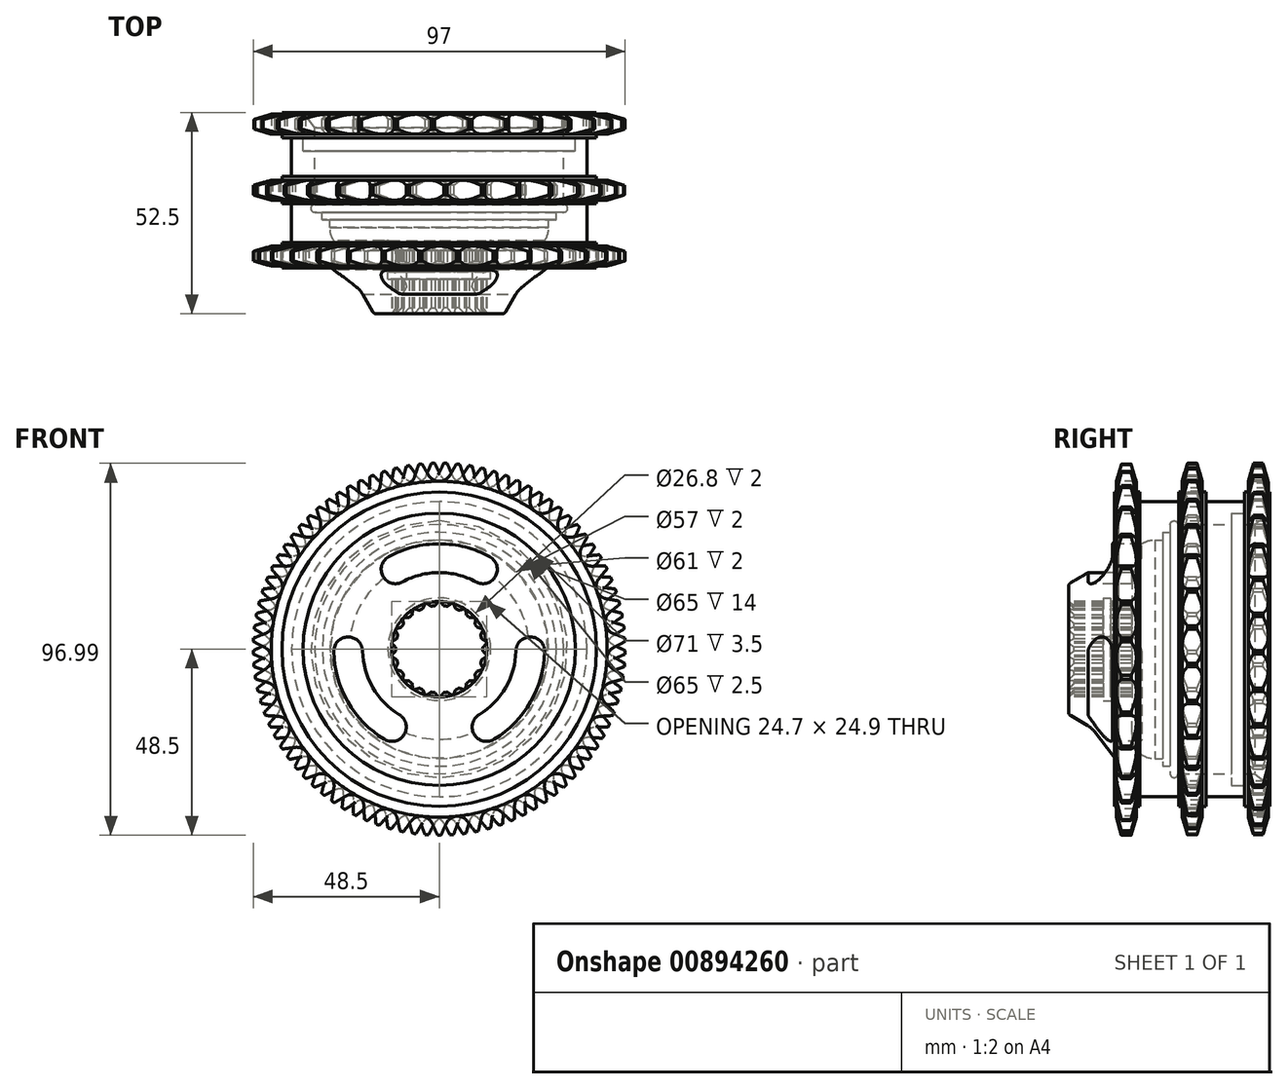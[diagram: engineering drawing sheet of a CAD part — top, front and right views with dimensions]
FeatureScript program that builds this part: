
annotation { "Feature Type Name" : "Feature", "Feature Type Description" : "" }
export const myFeature = defineFeature(function(context is Context, id is Id, definition is map)
    precondition{}
    {
        {
            var Q0;
            Q0=qCreatedBy(makeId("Right.planeOp"),FACE);
            var sketch = newSketch(context, id + "F0", { "sketchPlane" : qUnion([Q0])});
            skLineSegment(sketch, "E0.MirrorCS", {"start": v(34.85, 43.8) * mm, "end": v(34.85, 41) * mm});
            skLineSegment(sketch, "E1.MirrorCS", {"start": v(17.65, 41) * mm, "end": v(17.65, 43.8) * mm});
            skLineSegment(sketch, "E2.MirrorCS", {"start": v(5, 19.92) * mm, "end": v(0.5, 17.29) * mm});
            skLineSegment(sketch, "E3.MirrorCS", {"start": v(26.5, 32.5) * mm, "end": v(26.5, 30.5) * mm});
            skLineSegment(sketch, "E4.MirrorCS", {"start": v(35.8, 41) * mm, "end": v(34.85, 41) * mm});
            skLineSegment(sketch, "E5.MirrorCS", {"start": v(24.5, 28.5) * mm, "end": v(22.5, 28.5) * mm});
            skArc(sketch, "E6.MirrorCS", {"start": v(6.71, 21.41) * mm, "mid": v(5.93, 20.58) * mm, "end": v(5, 19.92) * mm});
            skLineSegment(sketch, "E7.MirrorCS", {"start": v(13, 34.5) * mm, "end": v(13, 31.56) * mm});
            skLineSegment(sketch, "E8.MirrorCS", {"start": v(9, 11.4) * mm, "end": v(9, 13.4) * mm});
            skLineSegment(sketch, "E9.MirrorCS", {"start": v(11, 13.4) * mm, "end": v(11, 11.4) * mm});
            skLineSegment(sketch, "E10.MirrorCS", {"start": v(33.5, 48.5) * mm, "end": v(31, 48.5) * mm});
            skArc(sketch, "E11.MirrorCS", {"start": v(12, 35.5) * mm, "mid": v(12.7, 35.2) * mm, "end": v(13, 34.5) * mm});
            skLineSegment(sketch, "E12.MirrorCS", {"start": v(29.65, 41) * mm, "end": v(28.7, 41) * mm});
            skLineSegment(sketch, "E13.MirrorCS", {"start": v(46.85, 43.8) * mm, "end": v(46.85, 41) * mm});
            skArc(sketch, "E14.MirrorCS", {"start": v(26.5, 32.5) * mm, "mid": v(27.5, 33.5) * mm, "end": v(28.5, 32.5) * mm});
            skLineSegment(sketch, "E15.MirrorCS", {"start": v(0, 12.45) * mm, "end": v(0, 16.43) * mm});
            skLineSegment(sketch, "E16.MirrorCS", {"start": v(46.85, 41) * mm, "end": v(45.9, 41) * mm});
            skLineSegment(sketch, "E17.MirrorCS", {"start": v(26.5, 30.5) * mm, "end": v(24.5, 30.5) * mm});
            skLineSegment(sketch, "E18.MirrorCS", {"start": v(1.5, 11.4) * mm, "end": v(0, 12.45) * mm});
            skLineSegment(sketch, "E19.MirrorCS", {"start": v(24.5, 30.5) * mm, "end": v(24.5, 28.5) * mm});
            skArc(sketch, "E20.MirrorCS", {"start": v(0, 16.43) * mm, "mid": v(0.13, 16.92) * mm, "end": v(0.5, 17.29) * mm});
            skLineSegment(sketch, "E21.MirrorCS", {"start": v(18.6, 41) * mm, "end": v(17.65, 41) * mm});
            skLineSegment(sketch, "E22.MirrorCS", {"start": v(29.65, 43.8) * mm, "end": v(29.65, 41) * mm});
            skLineSegment(sketch, "E23.MirrorCS", {"start": v(9, 13.4) * mm, "end": v(11, 13.4) * mm});
            skLineSegment(sketch, "E24.MirrorCS", {"start": v(18.6, 38.5) * mm, "end": v(18.6, 41) * mm});
            skLineSegment(sketch, "E25.MirrorCS", {"start": v(48.5, 32.5) * mm, "end": v(46, 32.5) * mm});
            skLineSegment(sketch, "E26.MirrorCS", {"start": v(42.5, 35.5) * mm, "end": v(46, 35.5) * mm});
            skLineSegment(sketch, "E27.MirrorCS", {"start": v(12.45, 43.8) * mm, "end": v(12.45, 41) * mm});
            skLineSegment(sketch, "E28.MirrorCS", {"start": v(52.05, 41) * mm, "end": v(52.5, 41) * mm});
            skLineSegment(sketch, "E29.MirrorCS", {"start": v(48.5, 32.5) * mm, "end": v(52.5, 35.5) * mm});
            skLineSegment(sketch, "E30.MirrorCS", {"start": v(42.5, 32.5) * mm, "end": v(42.5, 35.5) * mm});
            skArc(sketch, "E31.MirrorCS", {"start": v(13, 31.56) * mm, "mid": v(12.68, 29.61) * mm, "end": v(11.74, 27.88) * mm});
            skLineSegment(sketch, "E32.MirrorCS", {"start": v(28.7, 41) * mm, "end": v(28.7, 38.5) * mm});
            skLineSegment(sketch, "E33.MirrorCS", {"start": v(52.05, 41) * mm, "end": v(52.05, 43.8) * mm});
            skLineSegment(sketch, "E34.MirrorCS", {"start": v(46, 35.5) * mm, "end": v(46, 32.5) * mm});
            skLineSegment(sketch, "E35.MirrorCS", {"start": v(16.3, 48.5) * mm, "end": v(13.8, 48.5) * mm});
            skLineSegment(sketch, "E36.MirrorCS", {"start": v(35.8, 38.5) * mm, "end": v(35.8, 41) * mm});
            skLineSegment(sketch, "E37.MirrorCS", {"start": v(50.7, 48.5) * mm, "end": v(48.2, 48.5) * mm});
            skLineSegment(sketch, "E38.MirrorCS", {"start": v(12.45, 41) * mm, "end": v(12, 41) * mm});
            skLineSegment(sketch, "E39.MirrorCS", {"start": v(45.9, 41) * mm, "end": v(45.9, 38.5) * mm});
            skLineSegment(sketch, "E40.MirrorCS", {"start": v(33.5, 48.5) * mm, "end": v(34.85, 43.8) * mm});
            skLineSegment(sketch, "E41.MirrorCS", {"start": v(45.9, 38.5) * mm, "end": v(35.8, 38.5) * mm});
            skLineSegment(sketch, "E42.MirrorCS", {"start": v(34.85, 43.8) * mm, "end": v(29.65, 43.8) * mm, "construction": true});
            skLineSegment(sketch, "E43.MirrorCS", {"start": v(45.9, 41) * mm, "end": v(35.8, 41) * mm, "construction": true});
            skLineSegment(sketch, "E44.MirrorCS", {"start": v(12, 35.5) * mm, "end": v(12, 41) * mm});
            skLineSegment(sketch, "E45.MirrorCS", {"start": v(29.65, 43.8) * mm, "end": v(31, 48.5) * mm});
            skLineSegment(sketch, "E46.MirrorCS", {"start": v(42.5, 32.5) * mm, "end": v(28.5, 32.5) * mm});
            skLineSegment(sketch, "E47.MirrorCS", {"start": v(17.65, 43.8) * mm, "end": v(12.45, 43.8) * mm, "construction": true});
            skArc(sketch, "E48.MirrorCS", {"start": v(22.5, 28.5) * mm, "mid": v(18.58, 27.1) * mm, "end": v(16.5, 23.5) * mm});
            skLineSegment(sketch, "E49.MirrorCS", {"start": v(13.8, 48.5) * mm, "end": v(12.45, 43.8) * mm});
            skLineSegment(sketch, "E50.MirrorCS", {"start": v(53.5, 0) * mm, "end": v(0, 0) * mm, "construction": true});
            skLineSegment(sketch, "E51.MirrorCS", {"start": v(52.05, 43.8) * mm, "end": v(50.7, 48.5) * mm});
            skLineSegment(sketch, "E52.MirrorCS", {"start": v(16.3, 48.5) * mm, "end": v(17.65, 43.8) * mm});
            skLineSegment(sketch, "E53.MirrorCS", {"start": v(48.2, 48.5) * mm, "end": v(33.5, 48.5) * mm, "construction": true});
            skLineSegment(sketch, "E54.MirrorCS", {"start": v(46.85, 43.8) * mm, "end": v(48.2, 48.5) * mm});
            skLineSegment(sketch, "E55.MirrorCS", {"start": v(29.65, 43.8) * mm, "end": v(17.65, 43.8) * mm, "construction": true});
            skLineSegment(sketch, "E56.MirrorCS", {"start": v(28.7, 38.5) * mm, "end": v(18.6, 38.5) * mm});
            skLineSegment(sketch, "E57.MirrorCS", {"start": v(52.5, 41) * mm, "end": v(52.5, 35.5) * mm});
            skLineSegment(sketch, "E58.MirrorCS", {"start": v(31, 48.5) * mm, "end": v(16.3, 48.5) * mm, "construction": true});
            skLineSegment(sketch, "E59.MirrorCS", {"start": v(16.5, 11.4) * mm, "end": v(16.5, 23.5) * mm});
            skLineSegment(sketch, "E60.MirrorCS", {"start": v(46.85, 43.8) * mm, "end": v(34.85, 43.8) * mm, "construction": true});
            skLineSegment(sketch, "E61.MirrorCS", {"start": v(16.5, 11.4) * mm, "end": v(11, 11.4) * mm});
            skLineSegment(sketch, "E62.MirrorCS", {"start": v(11.74, 27.88) * mm, "end": v(6.71, 21.41) * mm});
            skLineSegment(sketch, "E63.MirrorCS", {"start": v(28.7, 41) * mm, "end": v(18.6, 41) * mm, "construction": true});
            skLineSegment(sketch, "E64.MirrorCS", {"start": v(52.05, 43.8) * mm, "end": v(46.85, 43.8) * mm, "construction": true});
            skLineSegment(sketch, "E65.MirrorCS", {"start": v(-190.05, 35.5) * mm, "end": v(-190.05, 35.5) * mm});
            skLineSegment(sketch, "E66.MirrorCS", {"start": v(9, 11.4) * mm, "end": v(1.5, 11.4) * mm});
            skSolve(sketch);
        }
        {
            var Q0;
            Q0=makeQuery(id+"F0.imprint","IMPRINT",FACE,{"disambiguationData":[TD([[makeQuery(id+"F0.imprint","IMPRINT",EDGE,{"derivedFrom":sQuery(id+"F0.wireOp",EDGE,"E0.MirrorCS")}),-1.0]])]});
            var Q1;
            Q1=sQuery(id+"F0.wireOp",EDGE,"E50.MirrorCS");
            revolve(context, id + "F1", {"surfaceOperationType" : NewSurfaceOperationType.NEW, "entities" : qUnion([Q0]), "axis" : qUnion([Q1]), "revolveType" : RevolveType.FULL});
        }
        {
            var Q0;
            Q0=makeQuery(id+"F1.opRevolve","SWEPT_FACE",FACE,{"disambiguationData":[OSD([sQuery(id+"F0.wireOp",EDGE,"E15.MirrorCS")])]});
            var sketch = newSketch(context, id + "F2", { "sketchPlane" : qUnion([Q0])});
            skArc(sketch, "E67", {"start": v(0.2, 12.45) * mm, "mid": v(0, 12.45) * mm, "end": v(-0.2, 12.45) * mm});
            skArc(sketch, "E68", {"start": v(2.1, 11.2) * mm, "mid": v(1.62, 11.28) * mm, "end": v(1.14, 11.34) * mm});
            skArc(sketch, "E69", {"start": v(5.18, 10.16) * mm, "mid": v(4.74, 10.37) * mm, "end": v(4.29, 10.56) * mm});
            skArc(sketch, "E70", {"start": v(7.83, 8.29) * mm, "mid": v(7.47, 8.62) * mm, "end": v(7.09, 8.93) * mm});
            skArc(sketch, "E71", {"start": v(9.85, 5.75) * mm, "mid": v(9.6, 6.16) * mm, "end": v(9.32, 6.57) * mm});
            skArc(sketch, "E72", {"start": v(11.07, 2.74) * mm, "mid": v(10.94, 3.21) * mm, "end": v(10.8, 3.68) * mm});
            skArc(sketch, "E73", {"start": v(11.39, -0.49) * mm, "mid": v(11.4, 0) * mm, "end": v(11.39, 0.49) * mm});
            skArc(sketch, "E74", {"start": v(10.8, -3.68) * mm, "mid": v(10.94, -3.21) * mm, "end": v(11.07, -2.74) * mm});
            skArc(sketch, "E75", {"start": v(9.32, -6.57) * mm, "mid": v(9.6, -6.16) * mm, "end": v(9.85, -5.75) * mm});
            skArc(sketch, "E76", {"start": v(7.09, -8.93) * mm, "mid": v(7.47, -8.62) * mm, "end": v(7.83, -8.29) * mm});
            skArc(sketch, "E77", {"start": v(4.29, -10.56) * mm, "mid": v(4.74, -10.37) * mm, "end": v(5.18, -10.16) * mm});
            skArc(sketch, "E78", {"start": v(1.14, -11.34) * mm, "mid": v(1.62, -11.28) * mm, "end": v(2.1, -11.2) * mm});
            skArc(sketch, "E79", {"start": v(-2.1, -11.2) * mm, "mid": v(-1.62, -11.28) * mm, "end": v(-1.14, -11.34) * mm});
            skArc(sketch, "E80", {"start": v(-5.18, -10.16) * mm, "mid": v(-4.74, -10.37) * mm, "end": v(-4.29, -10.56) * mm});
            skArc(sketch, "E81", {"start": v(-7.83, -8.29) * mm, "mid": v(-7.47, -8.62) * mm, "end": v(-7.09, -8.93) * mm});
            skArc(sketch, "E82", {"start": v(-9.85, -5.75) * mm, "mid": v(-9.6, -6.16) * mm, "end": v(-9.32, -6.57) * mm});
            skArc(sketch, "E83", {"start": v(-11.07, -2.74) * mm, "mid": v(-10.94, -3.21) * mm, "end": v(-10.8, -3.68) * mm});
            skArc(sketch, "E84", {"start": v(-11.39, 0.49) * mm, "mid": v(-11.4, 0) * mm, "end": v(-11.39, -0.49) * mm});
            skArc(sketch, "E85", {"start": v(-10.8, 3.68) * mm, "mid": v(-10.94, 3.21) * mm, "end": v(-11.07, 2.74) * mm});
            skArc(sketch, "E86", {"start": v(-9.32, 6.57) * mm, "mid": v(-9.6, 6.16) * mm, "end": v(-9.85, 5.75) * mm});
            skArc(sketch, "E87", {"start": v(-7.09, 8.93) * mm, "mid": v(-7.47, 8.62) * mm, "end": v(-7.83, 8.29) * mm});
            skArc(sketch, "E88", {"start": v(-4.29, 10.56) * mm, "mid": v(-4.74, 10.37) * mm, "end": v(-5.18, 10.16) * mm});
            skArc(sketch, "E89", {"start": v(-1.14, 11.34) * mm, "mid": v(-1.62, 11.28) * mm, "end": v(-2.1, 11.2) * mm});
            skLineSegment(sketch, "E90", {"start": v(-0.2, 12.45) * mm, "end": v(-1.14, 11.34) * mm});
            skLineSegment(sketch, "E91", {"start": v(0.2, 12.45) * mm, "end": v(1.14, 11.34) * mm});
            skArc(sketch, "E92", {"start": v(3.7, 11.89) * mm, "mid": v(3.5, 11.95) * mm, "end": v(3.31, 12) * mm});
            skLineSegment(sketch, "E93", {"start": v(3.31, 12) * mm, "end": v(2.1, 11.2) * mm});
            skLineSegment(sketch, "E94", {"start": v(3.7, 11.89) * mm, "end": v(4.29, 10.56) * mm});
            skArc(sketch, "E95", {"start": v(6.9, 10.36) * mm, "mid": v(6.73, 10.47) * mm, "end": v(6.56, 10.58) * mm});
            skLineSegment(sketch, "E96", {"start": v(6.56, 10.58) * mm, "end": v(5.18, 10.16) * mm});
            skLineSegment(sketch, "E97", {"start": v(6.9, 10.36) * mm, "end": v(7.09, 8.93) * mm});
            skArc(sketch, "E98", {"start": v(9.54, 8) * mm, "mid": v(9.4, 8.15) * mm, "end": v(9.28, 8.3) * mm});
            skLineSegment(sketch, "E99", {"start": v(9.28, 8.3) * mm, "end": v(7.83, 8.29) * mm});
            skLineSegment(sketch, "E100", {"start": v(9.54, 8) * mm, "end": v(9.32, 6.57) * mm});
            skArc(sketch, "E101", {"start": v(11.4, 4.99) * mm, "mid": v(11.32, 5.17) * mm, "end": v(11.24, 5.35) * mm});
            skLineSegment(sketch, "E102", {"start": v(11.24, 5.35) * mm, "end": v(9.85, 5.75) * mm});
            skLineSegment(sketch, "E103", {"start": v(11.4, 4.99) * mm, "end": v(10.8, 3.68) * mm});
            skArc(sketch, "E104", {"start": v(12.35, 1.57) * mm, "mid": v(12.32, 1.77) * mm, "end": v(12.3, 1.97) * mm});
            skLineSegment(sketch, "E105", {"start": v(12.3, 1.97) * mm, "end": v(11.07, 2.74) * mm});
            skLineSegment(sketch, "E106", {"start": v(12.35, 1.57) * mm, "end": v(11.39, 0.49) * mm});
            skArc(sketch, "E107", {"start": v(12.3, -1.97) * mm, "mid": v(12.32, -1.77) * mm, "end": v(12.35, -1.57) * mm});
            skLineSegment(sketch, "E108", {"start": v(12.35, -1.57) * mm, "end": v(11.39, -0.49) * mm});
            skLineSegment(sketch, "E109", {"start": v(12.3, -1.97) * mm, "end": v(11.07, -2.74) * mm});
            skArc(sketch, "E110", {"start": v(11.24, -5.35) * mm, "mid": v(11.32, -5.17) * mm, "end": v(11.4, -4.99) * mm});
            skLineSegment(sketch, "E111", {"start": v(11.4, -4.99) * mm, "end": v(10.8, -3.68) * mm});
            skLineSegment(sketch, "E112", {"start": v(11.24, -5.35) * mm, "end": v(9.85, -5.75) * mm});
            skArc(sketch, "E113", {"start": v(9.28, -8.3) * mm, "mid": v(9.4, -8.15) * mm, "end": v(9.54, -8) * mm});
            skLineSegment(sketch, "E114", {"start": v(9.54, -8) * mm, "end": v(9.32, -6.57) * mm});
            skLineSegment(sketch, "E115", {"start": v(9.28, -8.3) * mm, "end": v(7.83, -8.29) * mm});
            skArc(sketch, "E116", {"start": v(6.56, -10.58) * mm, "mid": v(6.73, -10.47) * mm, "end": v(6.9, -10.36) * mm});
            skLineSegment(sketch, "E117", {"start": v(6.9, -10.36) * mm, "end": v(7.09, -8.93) * mm});
            skLineSegment(sketch, "E118", {"start": v(6.56, -10.58) * mm, "end": v(5.18, -10.16) * mm});
            skArc(sketch, "E119", {"start": v(3.31, -12) * mm, "mid": v(3.5, -11.95) * mm, "end": v(3.7, -11.89) * mm});
            skLineSegment(sketch, "E120", {"start": v(3.7, -11.89) * mm, "end": v(4.29, -10.56) * mm});
            skLineSegment(sketch, "E121", {"start": v(3.31, -12) * mm, "end": v(2.1, -11.2) * mm});
            skArc(sketch, "E122", {"start": v(-0.2, -12.45) * mm, "mid": v(0, -12.45) * mm, "end": v(0.2, -12.45) * mm});
            skLineSegment(sketch, "E123", {"start": v(0.2, -12.45) * mm, "end": v(1.14, -11.34) * mm});
            skLineSegment(sketch, "E124", {"start": v(-0.2, -12.45) * mm, "end": v(-1.14, -11.34) * mm});
            skArc(sketch, "E125", {"start": v(-3.7, -11.89) * mm, "mid": v(-3.5, -11.95) * mm, "end": v(-3.31, -12) * mm});
            skLineSegment(sketch, "E126", {"start": v(-3.31, -12) * mm, "end": v(-2.1, -11.2) * mm});
            skLineSegment(sketch, "E127", {"start": v(-3.7, -11.89) * mm, "end": v(-4.29, -10.56) * mm});
            skArc(sketch, "E128", {"start": v(-6.9, -10.36) * mm, "mid": v(-6.73, -10.47) * mm, "end": v(-6.56, -10.58) * mm});
            skLineSegment(sketch, "E129", {"start": v(-6.56, -10.58) * mm, "end": v(-5.18, -10.16) * mm});
            skLineSegment(sketch, "E130", {"start": v(-6.9, -10.36) * mm, "end": v(-7.09, -8.93) * mm});
            skArc(sketch, "E131", {"start": v(-9.54, -8) * mm, "mid": v(-9.4, -8.15) * mm, "end": v(-9.28, -8.3) * mm});
            skLineSegment(sketch, "E132", {"start": v(-9.28, -8.3) * mm, "end": v(-7.83, -8.29) * mm});
            skLineSegment(sketch, "E133", {"start": v(-9.54, -8) * mm, "end": v(-9.32, -6.57) * mm});
            skArc(sketch, "E134", {"start": v(-11.4, -4.99) * mm, "mid": v(-11.32, -5.17) * mm, "end": v(-11.24, -5.35) * mm});
            skLineSegment(sketch, "E135", {"start": v(-11.24, -5.35) * mm, "end": v(-9.85, -5.75) * mm});
            skLineSegment(sketch, "E136", {"start": v(-11.4, -4.99) * mm, "end": v(-10.8, -3.68) * mm});
            skArc(sketch, "E137", {"start": v(-12.35, -1.57) * mm, "mid": v(-12.32, -1.77) * mm, "end": v(-12.3, -1.97) * mm});
            skLineSegment(sketch, "E138", {"start": v(-12.3, -1.97) * mm, "end": v(-11.07, -2.74) * mm});
            skLineSegment(sketch, "E139", {"start": v(-12.35, -1.57) * mm, "end": v(-11.39, -0.49) * mm});
            skArc(sketch, "E140", {"start": v(-12.3, 1.97) * mm, "mid": v(-12.32, 1.77) * mm, "end": v(-12.35, 1.57) * mm});
            skLineSegment(sketch, "E141", {"start": v(-12.35, 1.57) * mm, "end": v(-11.39, 0.49) * mm});
            skLineSegment(sketch, "E142", {"start": v(-12.3, 1.97) * mm, "end": v(-11.07, 2.74) * mm});
            skArc(sketch, "E143", {"start": v(-11.24, 5.35) * mm, "mid": v(-11.32, 5.17) * mm, "end": v(-11.4, 4.99) * mm});
            skLineSegment(sketch, "E144", {"start": v(-11.4, 4.99) * mm, "end": v(-10.8, 3.68) * mm});
            skLineSegment(sketch, "E145", {"start": v(-11.24, 5.35) * mm, "end": v(-9.85, 5.75) * mm});
            skArc(sketch, "E146", {"start": v(-9.28, 8.3) * mm, "mid": v(-9.4, 8.15) * mm, "end": v(-9.54, 8) * mm});
            skLineSegment(sketch, "E147", {"start": v(-9.54, 8) * mm, "end": v(-9.32, 6.57) * mm});
            skLineSegment(sketch, "E148", {"start": v(-9.28, 8.3) * mm, "end": v(-7.83, 8.29) * mm});
            skArc(sketch, "E149", {"start": v(-6.56, 10.58) * mm, "mid": v(-6.73, 10.47) * mm, "end": v(-6.9, 10.36) * mm});
            skLineSegment(sketch, "E150", {"start": v(-6.9, 10.36) * mm, "end": v(-7.09, 8.93) * mm});
            skLineSegment(sketch, "E151", {"start": v(-6.56, 10.58) * mm, "end": v(-5.18, 10.16) * mm});
            skArc(sketch, "E152", {"start": v(-3.31, 12) * mm, "mid": v(-3.5, 11.95) * mm, "end": v(-3.7, 11.89) * mm});
            skLineSegment(sketch, "E153", {"start": v(-3.7, 11.89) * mm, "end": v(-4.29, 10.56) * mm});
            skLineSegment(sketch, "E154", {"start": v(-3.31, 12) * mm, "end": v(-2.1, 11.2) * mm});
            skSolve(sketch);
        }
        {
            var Q0;
            Q0 = qSketchRegion(id + "F2", true);
            extrude(context, id + "F3", {"entities" : qUnion([Q0]), "operationType" : NewBodyOperationType.REMOVE, "endBound" : BoundingType.THROUGH_ALL, "oppositeDirection" : true, "depth" : 25 * mm, "offsetDistance" : 25 * mm});
        }
        {
            var Q0;
            Q0=makeQuery(id+"F1.opRevolve","SWEPT_FACE",FACE,{"disambiguationData":[OSD([sQuery(id+"F0.wireOp",EDGE,"E15.MirrorCS")])]});
            var sketch = newSketch(context, id + "F4", { "sketchPlane" : qUnion([Q0])});
            skArc(sketch, "E155", {"start": v(13.2, 24.13) * mm, "mid": v(0, 27.5) * mm, "end": v(-13.2, 24.13) * mm});
            skArc(sketch, "E156", {"start": v(9.6, 17.55) * mm, "mid": v(0, 20) * mm, "end": v(-9.6, 17.55) * mm});
            skArc(sketch, "E157", {"start": v(-13.2, 24.13) * mm, "mid": v(-14.69, 19.04) * mm, "end": v(-9.6, 17.55) * mm});
            skArc(sketch, "E158", {"start": v(9.6, 17.55) * mm, "mid": v(14.69, 19.04) * mm, "end": v(13.2, 24.13) * mm});
            skCircle(sketch, "E159", {"center": v(0, 0) * mm, "radius": 23.75 * mm, "construction": true});
            skLineSegment(sketch, "E160", {"start": v(0, 0) * mm, "end": v(11.4, 20.84) * mm, "construction": true});
            skLineSegment(sketch, "E161", {"start": v(0, 0) * mm, "end": v(-11.4, 20.84) * mm, "construction": true});
            skLineSegment(sketch, "E162", {"start": v(0, 0) * mm, "end": v(0, 23.75) * mm});
            skArc(sketch, "E163.1.0", {"start": v(-20, -0.46) * mm, "mid": v(-23.83, 3.2) * mm, "end": v(-27.5, -0.64) * mm});
            skArc(sketch, "E163.1.1", {"start": v(-27.5, -0.64) * mm, "mid": v(-23.82, -13.75) * mm, "end": v(-14.3, -23.5) * mm});
            skArc(sketch, "E163.1.2", {"start": v(-14.3, -23.5) * mm, "mid": v(-9.14, -22.24) * mm, "end": v(-10.4, -17.08) * mm});
            skArc(sketch, "E163.1.3", {"start": v(-20, -0.46) * mm, "mid": v(-17.32, -10) * mm, "end": v(-10.4, -17.08) * mm});
            skArc(sketch, "E163.2.0", {"start": v(10.4, -17.08) * mm, "mid": v(9.14, -22.24) * mm, "end": v(14.3, -23.5) * mm});
            skArc(sketch, "E163.2.1", {"start": v(14.3, -23.5) * mm, "mid": v(23.82, -13.75) * mm, "end": v(27.5, -0.64) * mm});
            skArc(sketch, "E163.2.2", {"start": v(27.5, -0.64) * mm, "mid": v(23.83, 3.2) * mm, "end": v(20, -0.46) * mm});
            skArc(sketch, "E163.2.3", {"start": v(10.4, -17.08) * mm, "mid": v(17.32, -10) * mm, "end": v(20, -0.46) * mm});
            skSolve(sketch);
        }
        {
            var Q0;
            Q0 = qSketchRegion(id + "F4", true);
            extrude(context, id + "F5", {"entities" : qUnion([Q0]), "operationType" : NewBodyOperationType.REMOVE, "endBound" : BoundingType.THROUGH_ALL, "oppositeDirection" : true, "depth" : 25 * mm, "offsetDistance" : 25 * mm});
        }
        {
            var Q0;
            Q0=makeQuery(id+"F1.opRevolve","SWEPT_FACE",FACE,{"disambiguationData":[OSD([sQuery(id+"F0.wireOp",EDGE,"E27.MirrorCS")])]});
            var sketch = newSketch(context, id + "F6", { "sketchPlane" : qUnion([Q0])});
            skArc(sketch, "E164", {"start": v(5.36, 48.2) * mm, "mid": v(4.9, 48.25) * mm, "end": v(4.45, 48.3) * mm});
            skArc(sketch, "E165", {"start": v(0, 43.8) * mm, "mid": v(1.6, 44.23) * mm, "end": v(2.77, 45.4) * mm});
            skLineSegment(sketch, "E166", {"start": v(4.46, 48.3) * mm, "end": v(2.77, 45.4) * mm});
            skArc(sketch, "E167", {"start": v(-4.45, 48.3) * mm, "mid": v(-4.9, 48.25) * mm, "end": v(-5.36, 48.2) * mm});
            skArc(sketch, "E168", {"start": v(-2.77, 45.4) * mm, "mid": v(-1.6, 44.23) * mm, "end": v(0, 43.8) * mm});
            skLineSegment(sketch, "E169", {"start": v(-4.46, 48.3) * mm, "end": v(-2.77, 45.4) * mm});
            skArc(sketch, "E170.1.0", {"start": v(-14.08, 46.41) * mm, "mid": v(-14.52, 46.28) * mm, "end": v(-14.95, 46.14) * mm});
            skLineSegment(sketch, "E170.1.1", {"start": v(-14.1, 46.42) * mm, "end": v(-11.85, 43.9) * mm});
            skArc(sketch, "E170.1.2", {"start": v(-11.85, 43.9) * mm, "mid": v(-10.47, 43) * mm, "end": v(-8.82, 42.9) * mm});
            skArc(sketch, "E170.1.3", {"start": v(-8.82, 42.9) * mm, "mid": v(-7.34, 43.64) * mm, "end": v(-6.43, 45.02) * mm});
            skLineSegment(sketch, "E170.1.4", {"start": v(-5.36, 48.22) * mm, "end": v(-6.43, 45.02) * mm});
            skArc(sketch, "E170.2.0", {"start": v(-23.14, 42.63) * mm, "mid": v(-23.54, 42.4) * mm, "end": v(-23.94, 42.18) * mm});
            skLineSegment(sketch, "E170.2.1", {"start": v(-23.15, 42.63) * mm, "end": v(-20.44, 40.62) * mm});
            skArc(sketch, "E170.2.2", {"start": v(-20.44, 40.62) * mm, "mid": v(-18.9, 40.01) * mm, "end": v(-17.27, 40.25) * mm});
            skArc(sketch, "E170.2.3", {"start": v(-17.27, 40.25) * mm, "mid": v(-15.97, 41.27) * mm, "end": v(-15.36, 42.8) * mm});
            skLineSegment(sketch, "E170.2.4", {"start": v(-14.95, 46.15) * mm, "end": v(-15.36, 42.8) * mm});
            skArc(sketch, "E170.2.5", {"start": v(-14.08, 46.41) * mm, "mid": v(-14.52, 46.28) * mm, "end": v(-14.95, 46.14) * mm});
            skArc(sketch, "E170.3.0", {"start": v(-31.24, 37.1) * mm, "mid": v(-31.6, 36.8) * mm, "end": v(-31.94, 36.5) * mm});
            skLineSegment(sketch, "E170.3.1", {"start": v(-31.26, 37.1) * mm, "end": v(-28.2, 35.68) * mm});
            skArc(sketch, "E170.3.2", {"start": v(-28.2, 35.68) * mm, "mid": v(-26.58, 35.39) * mm, "end": v(-25.02, 35.95) * mm});
            skArc(sketch, "E170.3.3", {"start": v(-25.02, 35.95) * mm, "mid": v(-23.95, 37.21) * mm, "end": v(-23.66, 38.84) * mm});
            skLineSegment(sketch, "E170.3.4", {"start": v(-23.94, 42.2) * mm, "end": v(-23.66, 38.84) * mm});
            skArc(sketch, "E170.3.5", {"start": v(-23.14, 42.63) * mm, "mid": v(-23.54, 42.4) * mm, "end": v(-23.94, 42.18) * mm});
            skArc(sketch, "E170.4.0", {"start": v(-38.07, 30.05) * mm, "mid": v(-38.35, 29.69) * mm, "end": v(-38.63, 29.32) * mm});
            skLineSegment(sketch, "E170.4.1", {"start": v(-38.09, 30.05) * mm, "end": v(-34.8, 29.27) * mm});
            skArc(sketch, "E170.4.2", {"start": v(-34.8, 29.27) * mm, "mid": v(-33.16, 29.31) * mm, "end": v(-31.75, 30.18) * mm});
            skArc(sketch, "E170.4.3", {"start": v(-31.75, 30.18) * mm, "mid": v(-30.96, 31.63) * mm, "end": v(-31, 33.28) * mm});
            skLineSegment(sketch, "E170.4.4", {"start": v(-31.94, 36.52) * mm, "end": v(-31, 33.28) * mm});
            skArc(sketch, "E170.4.5", {"start": v(-31.24, 37.1) * mm, "mid": v(-31.6, 36.8) * mm, "end": v(-31.94, 36.5) * mm});
            skArc(sketch, "E170.5.0", {"start": v(-43.34, 21.77) * mm, "mid": v(-43.54, 21.36) * mm, "end": v(-43.74, 20.95) * mm});
            skLineSegment(sketch, "E170.5.1", {"start": v(-43.36, 21.77) * mm, "end": v(-39.99, 21.66) * mm});
            skArc(sketch, "E170.5.2", {"start": v(-39.99, 21.66) * mm, "mid": v(-38.38, 22.04) * mm, "end": v(-37.17, 23.17) * mm});
            skArc(sketch, "E170.5.3", {"start": v(-37.17, 23.17) * mm, "mid": v(-36.69, 24.75) * mm, "end": v(-37.06, 26.36) * mm});
            skLineSegment(sketch, "E170.5.4", {"start": v(-38.64, 29.34) * mm, "end": v(-37.06, 26.36) * mm});
            skArc(sketch, "E170.5.5", {"start": v(-38.07, 30.05) * mm, "mid": v(-38.35, 29.69) * mm, "end": v(-38.63, 29.32) * mm});
            skArc(sketch, "E170.6.0", {"start": v(-46.84, 12.6) * mm, "mid": v(-46.95, 12.16) * mm, "end": v(-47.06, 11.71) * mm});
            skLineSegment(sketch, "E170.6.1", {"start": v(-46.85, 12.6) * mm, "end": v(-43.53, 13.17) * mm});
            skArc(sketch, "E170.6.2", {"start": v(-43.53, 13.17) * mm, "mid": v(-42.03, 13.86) * mm, "end": v(-41.07, 15.21) * mm});
            skArc(sketch, "E170.6.3", {"start": v(-41.07, 15.21) * mm, "mid": v(-40.92, 16.86) * mm, "end": v(-41.6, 18.36) * mm});
            skLineSegment(sketch, "E170.6.4", {"start": v(-43.75, 20.96) * mm, "end": v(-41.6, 18.36) * mm});
            skArc(sketch, "E170.6.5", {"start": v(-43.34, 21.77) * mm, "mid": v(-43.54, 21.36) * mm, "end": v(-43.74, 20.95) * mm});
            skArc(sketch, "E170.7.0", {"start": v(-48.41, 2.91) * mm, "mid": v(-48.44, 2.46) * mm, "end": v(-48.46, 2) * mm});
            skLineSegment(sketch, "E170.7.1", {"start": v(-48.43, 2.9) * mm, "end": v(-45.29, 4.14) * mm});
            skArc(sketch, "E170.7.2", {"start": v(-45.29, 4.14) * mm, "mid": v(-43.96, 5.12) * mm, "end": v(-43.3, 6.63) * mm});
            skArc(sketch, "E170.7.3", {"start": v(-43.3, 6.63) * mm, "mid": v(-43.48, 8.28) * mm, "end": v(-44.45, 9.6) * mm});
            skLineSegment(sketch, "E170.7.4", {"start": v(-47.08, 11.72) * mm, "end": v(-44.45, 9.6) * mm});
            skArc(sketch, "E170.7.5", {"start": v(-46.84, 12.6) * mm, "mid": v(-46.95, 12.16) * mm, "end": v(-47.06, 11.71) * mm});
            skArc(sketch, "E170.8.0", {"start": v(-48, -6.9) * mm, "mid": v(-47.94, -7.34) * mm, "end": v(-47.87, -7.8) * mm});
            skLineSegment(sketch, "E170.8.1", {"start": v(-48.02, -6.9) * mm, "end": v(-45.2, -5.06) * mm});
            skArc(sketch, "E170.8.2", {"start": v(-45.2, -5.06) * mm, "mid": v(-44.09, -3.83) * mm, "end": v(-43.74, -2.22) * mm});
            skArc(sketch, "E170.8.3", {"start": v(-43.74, -2.22) * mm, "mid": v(-44.25, -0.65) * mm, "end": v(-45.48, 0.47) * mm});
            skLineSegment(sketch, "E170.8.4", {"start": v(-48.47, 2) * mm, "end": v(-45.48, 0.47) * mm});
            skArc(sketch, "E170.8.5", {"start": v(-48.41, 2.91) * mm, "mid": v(-48.44, 2.46) * mm, "end": v(-48.46, 2) * mm});
            skArc(sketch, "E170.9.0", {"start": v(-45.64, -16.42) * mm, "mid": v(-45.48, -16.84) * mm, "end": v(-45.32, -17.27) * mm});
            skLineSegment(sketch, "E170.9.1", {"start": v(-45.65, -16.43) * mm, "end": v(-43.25, -14.06) * mm});
            skArc(sketch, "E170.9.2", {"start": v(-43.25, -14.06) * mm, "mid": v(-42.41, -12.63) * mm, "end": v(-42.4, -10.98) * mm});
            skArc(sketch, "E170.9.3", {"start": v(-42.4, -10.98) * mm, "mid": v(-43.22, -9.54) * mm, "end": v(-44.64, -8.7) * mm});
            skLineSegment(sketch, "E170.9.4", {"start": v(-47.89, -7.8) * mm, "end": v(-44.64, -8.7) * mm});
            skArc(sketch, "E170.9.5", {"start": v(-48, -6.9) * mm, "mid": v(-47.94, -7.34) * mm, "end": v(-47.87, -7.8) * mm});
            skArc(sketch, "E170.10.0", {"start": v(-41.4, -25.27) * mm, "mid": v(-41.16, -25.66) * mm, "end": v(-40.92, -26.04) * mm});
            skLineSegment(sketch, "E170.10.1", {"start": v(-41.4, -25.28) * mm, "end": v(-39.54, -22.48) * mm});
            skArc(sketch, "E170.10.2", {"start": v(-39.54, -22.48) * mm, "mid": v(-39, -20.91) * mm, "end": v(-39.32, -19.29) * mm});
            skArc(sketch, "E170.10.3", {"start": v(-39.32, -19.29) * mm, "mid": v(-40.41, -18.04) * mm, "end": v(-41.97, -17.5) * mm});
            skLineSegment(sketch, "E170.10.4", {"start": v(-45.34, -17.27) * mm, "end": v(-41.97, -17.5) * mm});
            skArc(sketch, "E170.10.5", {"start": v(-45.64, -16.42) * mm, "mid": v(-45.48, -16.84) * mm, "end": v(-45.32, -17.27) * mm});
            skArc(sketch, "E170.11.0", {"start": v(-35.47, -33.08) * mm, "mid": v(-35.15, -33.42) * mm, "end": v(-34.84, -33.74) * mm});
            skLineSegment(sketch, "E170.11.1", {"start": v(-35.47, -33.1) * mm, "end": v(-34.2, -29.97) * mm});
            skArc(sketch, "E170.11.2", {"start": v(-34.2, -29.97) * mm, "mid": v(-34, -28.33) * mm, "end": v(-34.64, -26.81) * mm});
            skArc(sketch, "E170.11.3", {"start": v(-34.64, -26.81) * mm, "mid": v(-35.95, -25.8) * mm, "end": v(-37.6, -25.6) * mm});
            skLineSegment(sketch, "E170.11.4", {"start": v(-40.93, -26.04) * mm, "end": v(-37.6, -25.6) * mm});
            skArc(sketch, "E170.11.5", {"start": v(-41.4, -25.27) * mm, "mid": v(-41.16, -25.66) * mm, "end": v(-40.92, -26.04) * mm});
            skArc(sketch, "E170.12.0", {"start": v(-28.08, -39.54) * mm, "mid": v(-27.7, -39.8) * mm, "end": v(-27.33, -40.07) * mm});
            skLineSegment(sketch, "E170.12.1", {"start": v(-28.08, -39.56) * mm, "end": v(-27.47, -36.24) * mm});
            skArc(sketch, "E170.12.2", {"start": v(-27.47, -36.24) * mm, "mid": v(-27.6, -34.6) * mm, "end": v(-28.53, -33.23) * mm});
            skArc(sketch, "E170.12.3", {"start": v(-28.53, -33.23) * mm, "mid": v(-30.02, -32.52) * mm, "end": v(-31.67, -32.64) * mm});
            skLineSegment(sketch, "E170.12.4", {"start": v(-34.85, -33.75) * mm, "end": v(-31.67, -32.64) * mm});
            skArc(sketch, "E170.12.5", {"start": v(-35.47, -33.08) * mm, "mid": v(-35.15, -33.42) * mm, "end": v(-34.84, -33.74) * mm});
            skArc(sketch, "E170.13.0", {"start": v(-19.54, -44.39) * mm, "mid": v(-19.13, -44.57) * mm, "end": v(-18.7, -44.75) * mm});
            skLineSegment(sketch, "E170.13.1", {"start": v(-19.54, -44.4) * mm, "end": v(-19.6, -41.03) * mm});
            skArc(sketch, "E170.13.2", {"start": v(-19.6, -41.03) * mm, "mid": v(-20.07, -39.44) * mm, "end": v(-21.26, -38.3) * mm});
            skArc(sketch, "E170.13.3", {"start": v(-21.26, -38.3) * mm, "mid": v(-22.86, -37.9) * mm, "end": v(-24.45, -38.35) * mm});
            skLineSegment(sketch, "E170.13.4", {"start": v(-27.34, -40.07) * mm, "end": v(-24.45, -38.35) * mm});
            skArc(sketch, "E170.13.5", {"start": v(-28.08, -39.54) * mm, "mid": v(-27.7, -39.8) * mm, "end": v(-27.33, -40.07) * mm});
            skArc(sketch, "E170.14.0", {"start": v(-10.2, -47.41) * mm, "mid": v(-9.76, -47.5) * mm, "end": v(-9.31, -47.6) * mm});
            skLineSegment(sketch, "E170.14.1", {"start": v(-10.2, -47.43) * mm, "end": v(-10.95, -44.14) * mm});
            skArc(sketch, "E170.14.2", {"start": v(-10.95, -44.14) * mm, "mid": v(-11.72, -42.68) * mm, "end": v(-13.11, -41.8) * mm});
            skArc(sketch, "E170.14.3", {"start": v(-13.11, -41.8) * mm, "mid": v(-14.76, -41.72) * mm, "end": v(-16.23, -42.48) * mm});
            skLineSegment(sketch, "E170.14.4", {"start": v(-18.72, -44.76) * mm, "end": v(-16.23, -42.48) * mm});
            skArc(sketch, "E170.14.5", {"start": v(-19.54, -44.39) * mm, "mid": v(-19.13, -44.57) * mm, "end": v(-18.7, -44.75) * mm});
            skArc(sketch, "E170.15.0", {"start": v(-0.46, -48.5) * mm, "mid": v(0, -48.5) * mm, "end": v(0.46, -48.5) * mm});
            skLineSegment(sketch, "E170.15.1", {"start": v(-0.45, -48.51) * mm, "end": v(-1.84, -45.44) * mm});
            skArc(sketch, "E170.15.2", {"start": v(-1.84, -45.44) * mm, "mid": v(-2.89, -44.16) * mm, "end": v(-4.43, -43.58) * mm});
            skArc(sketch, "E170.15.3", {"start": v(-4.43, -43.58) * mm, "mid": v(-6.06, -43.84) * mm, "end": v(-7.35, -44.88) * mm});
            skLineSegment(sketch, "E170.15.4", {"start": v(-9.32, -47.61) * mm, "end": v(-7.35, -44.88) * mm});
            skArc(sketch, "E170.15.5", {"start": v(-10.2, -47.41) * mm, "mid": v(-9.76, -47.5) * mm, "end": v(-9.31, -47.6) * mm});
            skArc(sketch, "E170.16.0", {"start": v(9.32, -47.6) * mm, "mid": v(9.76, -47.5) * mm, "end": v(10.21, -47.41) * mm});
            skLineSegment(sketch, "E170.16.1", {"start": v(9.33, -47.61) * mm, "end": v(7.35, -44.88) * mm});
            skArc(sketch, "E170.16.2", {"start": v(7.35, -44.88) * mm, "mid": v(6.06, -43.84) * mm, "end": v(4.43, -43.58) * mm});
            skArc(sketch, "E170.16.3", {"start": v(4.43, -43.58) * mm, "mid": v(2.89, -44.16) * mm, "end": v(1.84, -45.44) * mm});
            skLineSegment(sketch, "E170.16.4", {"start": v(0.45, -48.51) * mm, "end": v(1.84, -45.44) * mm});
            skArc(sketch, "E170.16.5", {"start": v(-0.46, -48.5) * mm, "mid": v(0, -48.5) * mm, "end": v(0.46, -48.5) * mm});
            skArc(sketch, "E170.17.0", {"start": v(18.7, -44.75) * mm, "mid": v(19.13, -44.57) * mm, "end": v(19.55, -44.39) * mm});
            skLineSegment(sketch, "E170.17.1", {"start": v(18.72, -44.76) * mm, "end": v(16.23, -42.48) * mm});
            skArc(sketch, "E170.17.2", {"start": v(16.23, -42.48) * mm, "mid": v(14.76, -41.72) * mm, "end": v(13.11, -41.8) * mm});
            skArc(sketch, "E170.17.3", {"start": v(13.11, -41.8) * mm, "mid": v(11.72, -42.68) * mm, "end": v(10.95, -44.14) * mm});
            skLineSegment(sketch, "E170.17.4", {"start": v(10.2, -47.43) * mm, "end": v(10.95, -44.14) * mm});
            skArc(sketch, "E170.17.5", {"start": v(9.32, -47.6) * mm, "mid": v(9.76, -47.5) * mm, "end": v(10.21, -47.41) * mm});
            skArc(sketch, "E170.18.0", {"start": v(27.33, -40.07) * mm, "mid": v(27.7, -39.8) * mm, "end": v(28.08, -39.54) * mm});
            skLineSegment(sketch, "E170.18.1", {"start": v(27.34, -40.07) * mm, "end": v(24.45, -38.35) * mm});
            skArc(sketch, "E170.18.2", {"start": v(24.45, -38.35) * mm, "mid": v(22.86, -37.9) * mm, "end": v(21.26, -38.3) * mm});
            skArc(sketch, "E170.18.3", {"start": v(21.26, -38.3) * mm, "mid": v(20.07, -39.44) * mm, "end": v(19.6, -41.03) * mm});
            skLineSegment(sketch, "E170.18.4", {"start": v(19.55, -44.4) * mm, "end": v(19.6, -41.03) * mm});
            skArc(sketch, "E170.18.5", {"start": v(18.7, -44.75) * mm, "mid": v(19.13, -44.57) * mm, "end": v(19.55, -44.39) * mm});
            skArc(sketch, "E170.19.0", {"start": v(34.84, -33.74) * mm, "mid": v(35.15, -33.41) * mm, "end": v(35.47, -33.08) * mm});
            skLineSegment(sketch, "E170.19.1", {"start": v(34.85, -33.75) * mm, "end": v(31.67, -32.64) * mm});
            skArc(sketch, "E170.19.2", {"start": v(31.67, -32.64) * mm, "mid": v(30.02, -32.52) * mm, "end": v(28.53, -33.23) * mm});
            skArc(sketch, "E170.19.3", {"start": v(28.53, -33.23) * mm, "mid": v(27.6, -34.6) * mm, "end": v(27.47, -36.25) * mm});
            skLineSegment(sketch, "E170.19.4", {"start": v(28.08, -39.56) * mm, "end": v(27.47, -36.25) * mm});
            skArc(sketch, "E170.19.5", {"start": v(27.33, -40.07) * mm, "mid": v(27.7, -39.8) * mm, "end": v(28.08, -39.54) * mm});
            skArc(sketch, "E170.20.0", {"start": v(40.92, -26.04) * mm, "mid": v(41.16, -25.65) * mm, "end": v(41.4, -25.27) * mm});
            skLineSegment(sketch, "E170.20.1", {"start": v(40.93, -26.04) * mm, "end": v(37.59, -25.6) * mm});
            skArc(sketch, "E170.20.2", {"start": v(37.59, -25.6) * mm, "mid": v(35.95, -25.8) * mm, "end": v(34.64, -26.81) * mm});
            skArc(sketch, "E170.20.3", {"start": v(34.64, -26.81) * mm, "mid": v(34, -28.33) * mm, "end": v(34.2, -29.97) * mm});
            skLineSegment(sketch, "E170.20.4", {"start": v(35.47, -33.1) * mm, "end": v(34.2, -29.97) * mm});
            skArc(sketch, "E170.20.5", {"start": v(34.84, -33.74) * mm, "mid": v(35.15, -33.41) * mm, "end": v(35.47, -33.08) * mm});
            skArc(sketch, "E170.21.0", {"start": v(45.32, -17.27) * mm, "mid": v(45.48, -16.84) * mm, "end": v(45.64, -16.41) * mm});
            skLineSegment(sketch, "E170.21.1", {"start": v(45.34, -17.27) * mm, "end": v(41.97, -17.5) * mm});
            skArc(sketch, "E170.21.2", {"start": v(41.97, -17.5) * mm, "mid": v(40.4, -18.04) * mm, "end": v(39.32, -19.29) * mm});
            skArc(sketch, "E170.21.3", {"start": v(39.32, -19.29) * mm, "mid": v(39, -20.91) * mm, "end": v(39.54, -22.48) * mm});
            skLineSegment(sketch, "E170.21.4", {"start": v(41.4, -25.28) * mm, "end": v(39.54, -22.48) * mm});
            skArc(sketch, "E170.21.5", {"start": v(40.92, -26.04) * mm, "mid": v(41.16, -25.65) * mm, "end": v(41.4, -25.27) * mm});
            skArc(sketch, "E170.22.0", {"start": v(47.87, -7.8) * mm, "mid": v(47.94, -7.34) * mm, "end": v(48, -6.9) * mm});
            skLineSegment(sketch, "E170.22.1", {"start": v(47.89, -7.8) * mm, "end": v(44.64, -8.7) * mm});
            skArc(sketch, "E170.22.2", {"start": v(44.64, -8.7) * mm, "mid": v(43.21, -9.54) * mm, "end": v(42.4, -10.98) * mm});
            skArc(sketch, "E170.22.3", {"start": v(42.4, -10.98) * mm, "mid": v(42.41, -12.63) * mm, "end": v(43.25, -14.06) * mm});
            skLineSegment(sketch, "E170.22.4", {"start": v(45.65, -16.43) * mm, "end": v(43.25, -14.06) * mm});
            skArc(sketch, "E170.22.5", {"start": v(45.32, -17.27) * mm, "mid": v(45.48, -16.84) * mm, "end": v(45.64, -16.41) * mm});
            skArc(sketch, "E170.23.0", {"start": v(48.46, 2) * mm, "mid": v(48.44, 2.46) * mm, "end": v(48.41, 2.91) * mm});
            skLineSegment(sketch, "E170.23.1", {"start": v(48.47, 2) * mm, "end": v(45.47, 0.46) * mm});
            skArc(sketch, "E170.23.2", {"start": v(45.47, 0.46) * mm, "mid": v(44.25, -0.65) * mm, "end": v(43.74, -2.22) * mm});
            skArc(sketch, "E170.23.3", {"start": v(43.74, -2.22) * mm, "mid": v(44.09, -3.83) * mm, "end": v(45.2, -5.06) * mm});
            skLineSegment(sketch, "E170.23.4", {"start": v(48.02, -6.9) * mm, "end": v(45.2, -5.06) * mm});
            skArc(sketch, "E170.23.5", {"start": v(47.87, -7.8) * mm, "mid": v(47.94, -7.34) * mm, "end": v(48, -6.9) * mm});
            skArc(sketch, "E170.24.0", {"start": v(47.06, 11.71) * mm, "mid": v(46.95, 12.16) * mm, "end": v(46.84, 12.6) * mm});
            skLineSegment(sketch, "E170.24.1", {"start": v(47.08, 11.72) * mm, "end": v(44.45, 9.6) * mm});
            skArc(sketch, "E170.24.2", {"start": v(44.45, 9.6) * mm, "mid": v(43.47, 8.28) * mm, "end": v(43.3, 6.63) * mm});
            skArc(sketch, "E170.24.3", {"start": v(43.3, 6.63) * mm, "mid": v(43.96, 5.12) * mm, "end": v(45.29, 4.14) * mm});
            skLineSegment(sketch, "E170.24.4", {"start": v(48.43, 2.9) * mm, "end": v(45.29, 4.14) * mm});
            skArc(sketch, "E170.24.5", {"start": v(48.46, 2) * mm, "mid": v(48.44, 2.46) * mm, "end": v(48.41, 2.91) * mm});
            skArc(sketch, "E170.25.0", {"start": v(43.74, 20.95) * mm, "mid": v(43.54, 21.36) * mm, "end": v(43.34, 21.77) * mm});
            skLineSegment(sketch, "E170.25.1", {"start": v(43.75, 20.96) * mm, "end": v(41.6, 18.36) * mm});
            skArc(sketch, "E170.25.2", {"start": v(41.6, 18.36) * mm, "mid": v(40.92, 16.86) * mm, "end": v(41.07, 15.21) * mm});
            skArc(sketch, "E170.25.3", {"start": v(41.07, 15.21) * mm, "mid": v(42.03, 13.86) * mm, "end": v(43.53, 13.17) * mm});
            skLineSegment(sketch, "E170.25.4", {"start": v(46.85, 12.6) * mm, "end": v(43.53, 13.17) * mm});
            skArc(sketch, "E170.25.5", {"start": v(47.06, 11.71) * mm, "mid": v(46.95, 12.16) * mm, "end": v(46.84, 12.6) * mm});
            skArc(sketch, "E170.26.0", {"start": v(38.63, 29.33) * mm, "mid": v(38.35, 29.69) * mm, "end": v(38.07, 30.05) * mm});
            skLineSegment(sketch, "E170.26.1", {"start": v(38.64, 29.34) * mm, "end": v(37.06, 26.36) * mm});
            skArc(sketch, "E170.26.2", {"start": v(37.06, 26.36) * mm, "mid": v(36.69, 24.75) * mm, "end": v(37.17, 23.17) * mm});
            skArc(sketch, "E170.26.3", {"start": v(37.17, 23.17) * mm, "mid": v(38.38, 22.04) * mm, "end": v(39.99, 21.66) * mm});
            skLineSegment(sketch, "E170.26.4", {"start": v(43.36, 21.77) * mm, "end": v(39.99, 21.66) * mm});
            skArc(sketch, "E170.26.5", {"start": v(43.74, 20.95) * mm, "mid": v(43.54, 21.36) * mm, "end": v(43.34, 21.77) * mm});
            skArc(sketch, "E170.27.0", {"start": v(31.94, 36.5) * mm, "mid": v(31.6, 36.8) * mm, "end": v(31.24, 37.1) * mm});
            skLineSegment(sketch, "E170.27.1", {"start": v(31.94, 36.52) * mm, "end": v(31, 33.28) * mm});
            skArc(sketch, "E170.27.2", {"start": v(31, 33.28) * mm, "mid": v(30.96, 31.63) * mm, "end": v(31.75, 30.18) * mm});
            skArc(sketch, "E170.27.3", {"start": v(31.75, 30.18) * mm, "mid": v(33.16, 29.31) * mm, "end": v(34.8, 29.27) * mm});
            skLineSegment(sketch, "E170.27.4", {"start": v(38.09, 30.05) * mm, "end": v(34.8, 29.27) * mm});
            skArc(sketch, "E170.27.5", {"start": v(38.63, 29.33) * mm, "mid": v(38.35, 29.69) * mm, "end": v(38.07, 30.05) * mm});
            skArc(sketch, "E170.28.0", {"start": v(23.93, 42.18) * mm, "mid": v(23.54, 42.4) * mm, "end": v(23.14, 42.63) * mm});
            skLineSegment(sketch, "E170.28.1", {"start": v(23.94, 42.2) * mm, "end": v(23.66, 38.84) * mm});
            skArc(sketch, "E170.28.2", {"start": v(23.66, 38.84) * mm, "mid": v(23.95, 37.21) * mm, "end": v(25.02, 35.95) * mm});
            skArc(sketch, "E170.28.3", {"start": v(25.02, 35.95) * mm, "mid": v(26.58, 35.39) * mm, "end": v(28.2, 35.68) * mm});
            skLineSegment(sketch, "E170.28.4", {"start": v(31.26, 37.1) * mm, "end": v(28.2, 35.68) * mm});
            skArc(sketch, "E170.28.5", {"start": v(31.94, 36.5) * mm, "mid": v(31.6, 36.8) * mm, "end": v(31.24, 37.1) * mm});
            skArc(sketch, "E170.29.0", {"start": v(14.95, 46.14) * mm, "mid": v(14.52, 46.28) * mm, "end": v(14.08, 46.41) * mm});
            skLineSegment(sketch, "E170.29.1", {"start": v(14.95, 46.15) * mm, "end": v(15.36, 42.8) * mm});
            skArc(sketch, "E170.29.2", {"start": v(15.36, 42.8) * mm, "mid": v(15.97, 41.27) * mm, "end": v(17.27, 40.25) * mm});
            skArc(sketch, "E170.29.3", {"start": v(17.27, 40.25) * mm, "mid": v(18.9, 40.01) * mm, "end": v(20.44, 40.62) * mm});
            skLineSegment(sketch, "E170.29.4", {"start": v(23.15, 42.64) * mm, "end": v(20.44, 40.62) * mm});
            skArc(sketch, "E170.29.5", {"start": v(23.93, 42.18) * mm, "mid": v(23.54, 42.4) * mm, "end": v(23.14, 42.63) * mm});
            skLineSegment(sketch, "E170.30.1", {"start": v(5.35, 48.22) * mm, "end": v(6.43, 45.02) * mm});
            skArc(sketch, "E170.30.2", {"start": v(6.43, 45.02) * mm, "mid": v(7.34, 43.64) * mm, "end": v(8.82, 42.9) * mm});
            skArc(sketch, "E170.30.3", {"start": v(8.82, 42.9) * mm, "mid": v(10.47, 43) * mm, "end": v(11.85, 43.9) * mm});
            skLineSegment(sketch, "E170.30.4", {"start": v(14.1, 46.42) * mm, "end": v(11.85, 43.9) * mm});
            skArc(sketch, "E170.30.5", {"start": v(14.95, 46.14) * mm, "mid": v(14.52, 46.28) * mm, "end": v(14.08, 46.41) * mm});
            skCircle(sketch, "E171", {"center": v(0, 0) * mm, "radius": 53.18 * mm});
            skSolve(sketch);
        }
        {
            var Q0;
            Q0 = qSketchRegion(id + "F6", true);
            extrude(context, id + "F7", {"entities" : qUnion([Q0]), "operationType" : NewBodyOperationType.REMOVE, "oppositeDirection" : true, "depth" : 6 * mm, "offsetDistance" : 25 * mm});
        }
        {
            var Q0;
            Q0=makeQuery(id+"F1.opRevolve","SWEPT_FACE",FACE,{"disambiguationData":[OSD([sQuery(id+"F0.wireOp",EDGE,"E22.MirrorCS")])]});
            var sketch = newSketch(context, id + "F8", { "sketchPlane" : qUnion([Q0])});
            skArc(sketch, "E172", {"start": v(2.1, 48.45) * mm, "mid": v(1.64, 48.47) * mm, "end": v(1.18, 48.49) * mm});
            skArc(sketch, "E173", {"start": v(-2.96, 43.7) * mm, "mid": v(-2.2, 43.85) * mm, "end": v(-1.5, 44.17) * mm});
            skArc(sketch, "E174", {"start": v(-1.5, 44.17) * mm, "mid": v(-0.8, 44.74) * mm, "end": v(-0.3, 45.48) * mm});
            skArc(sketch, "E175", {"start": v(3.37, 45.35) * mm, "mid": v(4.38, 44.04) * mm, "end": v(5.9, 43.4) * mm});
            skLineSegment(sketch, "E176", {"start": v(1.19, 48.5) * mm, "end": v(-0.3, 45.48) * mm});
            skLineSegment(sketch, "E177", {"start": v(2.09, 48.47) * mm, "end": v(3.11, 45.99) * mm});
            skLineSegment(sketch, "E178", {"start": v(3.11, 45.99) * mm, "end": v(3.37, 45.35) * mm});
            skArc(sketch, "E179.1.0", {"start": v(-11.7, 42.21) * mm, "mid": v(-10.98, 42.5) * mm, "end": v(-10.35, 42.96) * mm});
            skArc(sketch, "E179.1.1", {"start": v(-10.35, 42.96) * mm, "mid": v(-9.8, 43.66) * mm, "end": v(-9.45, 44.49) * mm});
            skLineSegment(sketch, "E179.1.2", {"start": v(-8.6, 47.75) * mm, "end": v(-9.45, 44.49) * mm});
            skArc(sketch, "E179.1.3", {"start": v(-7.7, 47.88) * mm, "mid": v(-8.15, 47.8) * mm, "end": v(-8.6, 47.73) * mm});
            skLineSegment(sketch, "E179.1.4", {"start": v(-7.71, 47.9) * mm, "end": v(-6.2, 45.67) * mm});
            skLineSegment(sketch, "E179.1.5", {"start": v(-6.2, 45.67) * mm, "end": v(-5.83, 45.1) * mm});
            skArc(sketch, "E179.1.6", {"start": v(-5.83, 45.1) * mm, "mid": v(-4.58, 44.02) * mm, "end": v(-2.96, 43.7) * mm});
            skArc(sketch, "E179.2.0", {"start": v(-19.95, 39) * mm, "mid": v(-19.3, 39.43) * mm, "end": v(-18.8, 40) * mm});
            skArc(sketch, "E179.2.1", {"start": v(-18.8, 40) * mm, "mid": v(-18.38, 40.8) * mm, "end": v(-18.21, 41.67) * mm});
            skLineSegment(sketch, "E179.2.2", {"start": v(-18.03, 45.04) * mm, "end": v(-18.21, 41.67) * mm});
            skArc(sketch, "E179.2.3", {"start": v(-17.18, 45.35) * mm, "mid": v(-17.61, 45.19) * mm, "end": v(-18.04, 45.02) * mm});
            skLineSegment(sketch, "E179.2.4", {"start": v(-17.2, 45.36) * mm, "end": v(-15.28, 43.49) * mm});
            skLineSegment(sketch, "E179.2.5", {"start": v(-15.28, 43.49) * mm, "end": v(-14.79, 43) * mm});
            skArc(sketch, "E179.2.6", {"start": v(-14.79, 43) * mm, "mid": v(-13.35, 42.2) * mm, "end": v(-11.7, 42.21) * mm});
            skArc(sketch, "E179.3.0", {"start": v(-27.4, 34.18) * mm, "mid": v(-26.85, 34.73) * mm, "end": v(-26.46, 35.4) * mm});
            skArc(sketch, "E179.3.1", {"start": v(-26.46, 35.4) * mm, "mid": v(-26.22, 36.26) * mm, "end": v(-26.23, 37.15) * mm});
            skLineSegment(sketch, "E179.3.2", {"start": v(-26.73, 40.49) * mm, "end": v(-26.23, 37.15) * mm});
            skArc(sketch, "E179.3.3", {"start": v(-25.96, 40.97) * mm, "mid": v(-26.35, 40.72) * mm, "end": v(-26.73, 40.47) * mm});
            skLineSegment(sketch, "E179.3.4", {"start": v(-25.98, 40.97) * mm, "end": v(-23.72, 39.52) * mm});
            skLineSegment(sketch, "E179.3.5", {"start": v(-23.72, 39.52) * mm, "end": v(-23.14, 39.15) * mm});
            skArc(sketch, "E179.3.6", {"start": v(-23.14, 39.15) * mm, "mid": v(-21.57, 38.65) * mm, "end": v(-19.95, 39) * mm});
            skArc(sketch, "E179.4.0", {"start": v(-33.71, 27.96) * mm, "mid": v(-33.3, 28.62) * mm, "end": v(-33.04, 29.35) * mm});
            skArc(sketch, "E179.4.1", {"start": v(-33.04, 29.35) * mm, "mid": v(-32.98, 30.24) * mm, "end": v(-33.17, 31.11) * mm});
            skLineSegment(sketch, "E179.4.2", {"start": v(-34.33, 34.28) * mm, "end": v(-33.17, 31.11) * mm});
            skArc(sketch, "E179.4.3", {"start": v(-33.68, 34.9) * mm, "mid": v(-34, 34.58) * mm, "end": v(-34.33, 34.26) * mm});
            skLineSegment(sketch, "E179.4.4", {"start": v(-33.7, 34.9) * mm, "end": v(-31.19, 33.94) * mm});
            skLineSegment(sketch, "E179.4.5", {"start": v(-31.19, 33.94) * mm, "end": v(-30.55, 33.7) * mm});
            skArc(sketch, "E179.4.6", {"start": v(-30.55, 33.7) * mm, "mid": v(-28.9, 33.51) * mm, "end": v(-27.4, 34.18) * mm});
            skArc(sketch, "E179.5.0", {"start": v(-38.65, 20.6) * mm, "mid": v(-38.37, 21.33) * mm, "end": v(-38.27, 22.1) * mm});
            skArc(sketch, "E179.5.1", {"start": v(-38.27, 22.1) * mm, "mid": v(-38.4, 22.98) * mm, "end": v(-38.75, 23.8) * mm});
            skLineSegment(sketch, "E179.5.2", {"start": v(-40.53, 26.66) * mm, "end": v(-38.75, 23.8) * mm});
            skArc(sketch, "E179.5.3", {"start": v(-40.01, 27.4) * mm, "mid": v(-40.27, 27.03) * mm, "end": v(-40.52, 26.65) * mm});
            skLineSegment(sketch, "E179.5.4", {"start": v(-40.03, 27.41) * mm, "end": v(-37.38, 26.97) * mm});
            skLineSegment(sketch, "E179.5.5", {"start": v(-37.38, 26.97) * mm, "end": v(-36.7, 26.85) * mm});
            skArc(sketch, "E179.5.6", {"start": v(-36.7, 26.85) * mm, "mid": v(-35.06, 27) * mm, "end": v(-33.71, 27.96) * mm});
            skArc(sketch, "E179.6.0", {"start": v(-42, 12.4) * mm, "mid": v(-41.88, 13.17) * mm, "end": v(-41.94, 13.94) * mm});
            skArc(sketch, "E179.6.1", {"start": v(-41.94, 13.94) * mm, "mid": v(-42.23, 14.78) * mm, "end": v(-42.75, 15.51) * mm});
            skLineSegment(sketch, "E179.6.2", {"start": v(-45.07, 17.96) * mm, "end": v(-42.75, 15.51) * mm});
            skArc(sketch, "E179.6.3", {"start": v(-44.71, 18.8) * mm, "mid": v(-44.89, 18.37) * mm, "end": v(-45.06, 17.95) * mm});
            skLineSegment(sketch, "E179.6.4", {"start": v(-44.73, 18.8) * mm, "end": v(-42.04, 18.89) * mm});
            skLineSegment(sketch, "E179.6.5", {"start": v(-42.04, 18.89) * mm, "end": v(-41.36, 18.91) * mm});
            skArc(sketch, "E179.6.6", {"start": v(-41.36, 18.91) * mm, "mid": v(-39.78, 19.4) * mm, "end": v(-38.65, 20.6) * mm});
            skArc(sketch, "E179.7.0", {"start": v(-43.64, 3.7) * mm, "mid": v(-43.67, 4.47) * mm, "end": v(-43.89, 5.21) * mm});
            skArc(sketch, "E179.7.1", {"start": v(-43.89, 5.21) * mm, "mid": v(-44.35, 5.98) * mm, "end": v(-45, 6.59) * mm});
            skLineSegment(sketch, "E179.7.2", {"start": v(-47.76, 8.52) * mm, "end": v(-45, 6.59) * mm});
            skArc(sketch, "E179.7.3", {"start": v(-47.58, 9.4) * mm, "mid": v(-47.67, 8.96) * mm, "end": v(-47.75, 8.5) * mm});
            skLineSegment(sketch, "E179.7.4", {"start": v(-47.6, 9.4) * mm, "end": v(-44.98, 10.04) * mm});
            skLineSegment(sketch, "E179.7.5", {"start": v(-44.98, 10.04) * mm, "end": v(-44.32, 10.2) * mm});
            skArc(sketch, "E179.7.6", {"start": v(-44.32, 10.2) * mm, "mid": v(-42.87, 11) * mm, "end": v(-42, 12.4) * mm});
            skArc(sketch, "E179.8.0", {"start": v(-43.5, -5.17) * mm, "mid": v(-43.68, -4.41) * mm, "end": v(-44.04, -3.73) * mm});
            skArc(sketch, "E179.8.1", {"start": v(-44.04, -3.73) * mm, "mid": v(-44.64, -3.07) * mm, "end": v(-45.4, -2.6) * mm});
            skLineSegment(sketch, "E179.8.2", {"start": v(-48.5, -1.27) * mm, "end": v(-45.4, -2.6) * mm});
            skArc(sketch, "E179.8.3", {"start": v(-48.5, -0.36) * mm, "mid": v(-48.5, -0.82) * mm, "end": v(-48.48, -1.28) * mm});
            skLineSegment(sketch, "E179.8.4", {"start": v(-48.51, -0.37) * mm, "end": v(-46.08, 0.78) * mm});
            skLineSegment(sketch, "E179.8.5", {"start": v(-46.08, 0.78) * mm, "end": v(-45.46, 1.07) * mm});
            skArc(sketch, "E179.8.6", {"start": v(-45.46, 1.07) * mm, "mid": v(-44.2, 2.14) * mm, "end": v(-43.64, 3.7) * mm});
            skArc(sketch, "E179.9.0", {"start": v(-41.56, -13.82) * mm, "mid": v(-41.9, -13.12) * mm, "end": v(-42.39, -12.52) * mm});
            skArc(sketch, "E179.9.1", {"start": v(-42.39, -12.52) * mm, "mid": v(-43.1, -12) * mm, "end": v(-43.95, -11.7) * mm});
            skLineSegment(sketch, "E179.9.2", {"start": v(-47.25, -11) * mm, "end": v(-43.95, -11.7) * mm});
            skArc(sketch, "E179.9.3", {"start": v(-47.43, -10.12) * mm, "mid": v(-47.34, -10.56) * mm, "end": v(-47.23, -11) * mm});
            skLineSegment(sketch, "E179.9.4", {"start": v(-47.45, -10.13) * mm, "end": v(-45.3, -8.51) * mm});
            skLineSegment(sketch, "E179.9.5", {"start": v(-45.3, -8.51) * mm, "end": v(-44.75, -8.1) * mm});
            skArc(sketch, "E179.9.6", {"start": v(-44.75, -8.1) * mm, "mid": v(-43.73, -6.8) * mm, "end": v(-43.5, -5.17) * mm});
            skArc(sketch, "E179.10.0", {"start": v(-37.93, -21.9) * mm, "mid": v(-38.4, -21.28) * mm, "end": v(-39, -20.8) * mm});
            skArc(sketch, "E179.10.1", {"start": v(-39, -20.8) * mm, "mid": v(-39.81, -20.43) * mm, "end": v(-40.7, -20.3) * mm});
            skLineSegment(sketch, "E179.10.2", {"start": v(-44.07, -20.3) * mm, "end": v(-40.7, -20.3) * mm});
            skArc(sketch, "E179.10.3", {"start": v(-44.43, -19.46) * mm, "mid": v(-44.24, -19.88) * mm, "end": v(-44.05, -20.3) * mm});
            skLineSegment(sketch, "E179.10.4", {"start": v(-44.44, -19.47) * mm, "end": v(-42.66, -17.46) * mm});
            skLineSegment(sketch, "E179.10.5", {"start": v(-42.66, -17.46) * mm, "end": v(-42.2, -16.94) * mm});
            skArc(sketch, "E179.10.6", {"start": v(-42.2, -16.94) * mm, "mid": v(-41.47, -15.47) * mm, "end": v(-41.56, -13.82) * mm});
            skArc(sketch, "E179.11.0", {"start": v(-32.75, -29.09) * mm, "mid": v(-33.33, -28.57) * mm, "end": v(-34.01, -28.22) * mm});
            skArc(sketch, "E179.11.1", {"start": v(-34.01, -28.22) * mm, "mid": v(-34.89, -28.02) * mm, "end": v(-35.78, -28.08) * mm});
            skLineSegment(sketch, "E179.11.2", {"start": v(-39.08, -28.75) * mm, "end": v(-35.78, -28.08) * mm});
            skArc(sketch, "E179.11.3", {"start": v(-39.6, -28) * mm, "mid": v(-39.33, -28.38) * mm, "end": v(-39.06, -28.74) * mm});
            skLineSegment(sketch, "E179.11.4", {"start": v(-39.6, -28.02) * mm, "end": v(-38.27, -25.69) * mm});
            skLineSegment(sketch, "E179.11.5", {"start": v(-38.27, -25.69) * mm, "end": v(-37.93, -25.1) * mm});
            skArc(sketch, "E179.11.6", {"start": v(-37.93, -25.1) * mm, "mid": v(-37.5, -23.5) * mm, "end": v(-37.93, -21.9) * mm});
            skArc(sketch, "E179.12.0", {"start": v(-26.22, -35.08) * mm, "mid": v(-26.9, -34.7) * mm, "end": v(-27.64, -34.49) * mm});
            skArc(sketch, "E179.12.1", {"start": v(-27.64, -34.49) * mm, "mid": v(-28.53, -34.47) * mm, "end": v(-29.4, -34.7) * mm});
            skLineSegment(sketch, "E179.12.2", {"start": v(-32.5, -36.03) * mm, "end": v(-29.4, -34.7) * mm});
            skArc(sketch, "E179.12.3", {"start": v(-33.15, -35.4) * mm, "mid": v(-32.82, -35.71) * mm, "end": v(-32.48, -36.02) * mm});
            skLineSegment(sketch, "E179.12.4", {"start": v(-33.16, -35.42) * mm, "end": v(-32.32, -32.87) * mm});
            skLineSegment(sketch, "E179.12.5", {"start": v(-32.32, -32.87) * mm, "end": v(-32.1, -32.21) * mm});
            skArc(sketch, "E179.12.6", {"start": v(-32.1, -32.21) * mm, "mid": v(-32, -30.56) * mm, "end": v(-32.75, -29.09) * mm});
            skArc(sketch, "E179.13.0", {"start": v(-18.62, -39.64) * mm, "mid": v(-19.36, -39.4) * mm, "end": v(-20.13, -39.34) * mm});
            skArc(sketch, "E179.13.1", {"start": v(-20.13, -39.34) * mm, "mid": v(-21, -39.5) * mm, "end": v(-21.8, -39.9) * mm});
            skLineSegment(sketch, "E179.13.2", {"start": v(-24.58, -41.83) * mm, "end": v(-21.8, -39.9) * mm});
            skArc(sketch, "E179.13.3", {"start": v(-25.35, -41.35) * mm, "mid": v(-24.96, -41.59) * mm, "end": v(-24.56, -41.82) * mm});
            skLineSegment(sketch, "E179.13.4", {"start": v(-25.35, -41.37) * mm, "end": v(-25.04, -38.7) * mm});
            skLineSegment(sketch, "E179.13.5", {"start": v(-25.04, -38.7) * mm, "end": v(-24.96, -38.02) * mm});
            skArc(sketch, "E179.13.6", {"start": v(-24.96, -38.02) * mm, "mid": v(-25.2, -36.38) * mm, "end": v(-26.22, -35.08) * mm});
            skArc(sketch, "E179.14.0", {"start": v(-10.26, -42.58) * mm, "mid": v(-11.03, -42.5) * mm, "end": v(-11.8, -42.6) * mm});
            skArc(sketch, "E179.14.1", {"start": v(-11.8, -42.6) * mm, "mid": v(-12.62, -42.93) * mm, "end": v(-13.32, -43.48) * mm});
            skLineSegment(sketch, "E179.14.2", {"start": v(-15.65, -45.92) * mm, "end": v(-13.32, -43.48) * mm});
            skArc(sketch, "E179.14.3", {"start": v(-16.5, -45.6) * mm, "mid": v(-16.07, -45.76) * mm, "end": v(-15.64, -45.9) * mm});
            skLineSegment(sketch, "E179.14.4", {"start": v(-16.5, -45.62) * mm, "end": v(-16.74, -42.95) * mm});
            skLineSegment(sketch, "E179.14.5", {"start": v(-16.74, -42.95) * mm, "end": v(-16.8, -42.26) * mm});
            skArc(sketch, "E179.14.6", {"start": v(-16.8, -42.26) * mm, "mid": v(-17.36, -40.7) * mm, "end": v(-18.62, -39.64) * mm});
            skArc(sketch, "E179.15.0", {"start": v(-1.48, -43.78) * mm, "mid": v(-2.25, -43.84) * mm, "end": v(-2.98, -44.1) * mm});
            skArc(sketch, "E179.15.1", {"start": v(-2.98, -44.1) * mm, "mid": v(-3.72, -44.6) * mm, "end": v(-4.3, -45.27) * mm});
            skLineSegment(sketch, "E179.15.2", {"start": v(-6.09, -48.13) * mm, "end": v(-4.3, -45.27) * mm});
            skArc(sketch, "E179.15.3", {"start": v(-6.99, -48) * mm, "mid": v(-6.53, -48.06) * mm, "end": v(-6.08, -48.12) * mm});
            skLineSegment(sketch, "E179.15.4", {"start": v(-6.98, -48) * mm, "end": v(-7.75, -45.44) * mm});
            skLineSegment(sketch, "E179.15.5", {"start": v(-7.75, -45.44) * mm, "end": v(-7.94, -44.78) * mm});
            skArc(sketch, "E179.15.6", {"start": v(-7.94, -44.78) * mm, "mid": v(-8.8, -43.37) * mm, "end": v(-10.26, -42.58) * mm});
            skArc(sketch, "E179.16.0", {"start": v(7.36, -43.18) * mm, "mid": v(6.62, -43.4) * mm, "end": v(5.95, -43.8) * mm});
            skArc(sketch, "E179.16.1", {"start": v(5.95, -43.8) * mm, "mid": v(5.33, -44.43) * mm, "end": v(4.9, -45.21) * mm});
            skLineSegment(sketch, "E179.16.2", {"start": v(3.72, -48.37) * mm, "end": v(4.9, -45.21) * mm});
            skArc(sketch, "E179.16.3", {"start": v(2.82, -48.42) * mm, "mid": v(3.27, -48.39) * mm, "end": v(3.73, -48.36) * mm});
            skLineSegment(sketch, "E179.16.4", {"start": v(2.83, -48.43) * mm, "end": v(1.56, -46.07) * mm});
            skLineSegment(sketch, "E179.16.5", {"start": v(1.56, -46.07) * mm, "end": v(1.23, -45.46) * mm});
            skArc(sketch, "E179.16.6", {"start": v(1.23, -45.46) * mm, "mid": v(0.1, -44.26) * mm, "end": v(-1.48, -43.78) * mm});
            skArc(sketch, "E179.17.0", {"start": v(15.9, -40.81) * mm, "mid": v(15.22, -41.18) * mm, "end": v(14.65, -41.7) * mm});
            skArc(sketch, "E179.17.1", {"start": v(14.65, -41.7) * mm, "mid": v(14.16, -42.45) * mm, "end": v(13.9, -43.3) * mm});
            skLineSegment(sketch, "E179.17.2", {"start": v(13.39, -46.63) * mm, "end": v(13.9, -43.3) * mm});
            skArc(sketch, "E179.17.3", {"start": v(12.5, -46.86) * mm, "mid": v(12.95, -46.74) * mm, "end": v(13.39, -46.62) * mm});
            skLineSegment(sketch, "E179.17.4", {"start": v(12.52, -46.87) * mm, "end": v(10.8, -44.8) * mm});
            skLineSegment(sketch, "E179.17.5", {"start": v(10.8, -44.8) * mm, "end": v(10.36, -44.28) * mm});
            skArc(sketch, "E179.17.6", {"start": v(10.36, -44.28) * mm, "mid": v(9, -43.33) * mm, "end": v(7.36, -43.18) * mm});
            skArc(sketch, "E179.18.0", {"start": v(23.8, -36.77) * mm, "mid": v(23.2, -37.27) * mm, "end": v(22.74, -37.9) * mm});
            skArc(sketch, "E179.18.1", {"start": v(22.74, -37.9) * mm, "mid": v(22.42, -38.73) * mm, "end": v(22.34, -39.62) * mm});
            skLineSegment(sketch, "E179.18.2", {"start": v(22.5, -42.98) * mm, "end": v(22.34, -39.62) * mm});
            skArc(sketch, "E179.18.3", {"start": v(21.68, -43.38) * mm, "mid": v(22.1, -43.18) * mm, "end": v(22.5, -42.97) * mm});
            skLineSegment(sketch, "E179.18.4", {"start": v(21.7, -43.4) * mm, "end": v(19.6, -41.72) * mm});
            skLineSegment(sketch, "E179.18.5", {"start": v(19.6, -41.72) * mm, "end": v(19.06, -41.3) * mm});
            skArc(sketch, "E179.18.6", {"start": v(19.06, -41.3) * mm, "mid": v(17.55, -40.63) * mm, "end": v(15.9, -40.81) * mm});
            skArc(sketch, "E179.19.0", {"start": v(30.7, -31.23) * mm, "mid": v(30.23, -31.84) * mm, "end": v(29.9, -32.54) * mm});
            skArc(sketch, "E179.19.1", {"start": v(29.9, -32.54) * mm, "mid": v(29.75, -33.42) * mm, "end": v(29.85, -34.3) * mm});
            skLineSegment(sketch, "E179.19.2", {"start": v(30.7, -37.57) * mm, "end": v(29.85, -34.3) * mm});
            skArc(sketch, "E179.19.3", {"start": v(29.97, -38.13) * mm, "mid": v(30.33, -37.85) * mm, "end": v(30.69, -37.56) * mm});
            skLineSegment(sketch, "E179.19.4", {"start": v(29.99, -38.14) * mm, "end": v(27.6, -36.92) * mm});
            skLineSegment(sketch, "E179.19.5", {"start": v(27.6, -36.92) * mm, "end": v(26.98, -36.6) * mm});
            skArc(sketch, "E179.19.6", {"start": v(26.98, -36.6) * mm, "mid": v(25.37, -36.27) * mm, "end": v(23.8, -36.77) * mm});
            skArc(sketch, "E179.20.0", {"start": v(36.37, -24.41) * mm, "mid": v(36.02, -25.1) * mm, "end": v(35.84, -25.86) * mm});
            skArc(sketch, "E179.20.1", {"start": v(35.84, -25.86) * mm, "mid": v(35.87, -26.75) * mm, "end": v(36.15, -27.6) * mm});
            skLineSegment(sketch, "E179.20.2", {"start": v(37.63, -30.63) * mm, "end": v(36.15, -27.6) * mm});
            skArc(sketch, "E179.20.3", {"start": v(37.04, -31.32) * mm, "mid": v(37.33, -30.97) * mm, "end": v(37.62, -30.61) * mm});
            skLineSegment(sketch, "E179.20.4", {"start": v(37.05, -31.32) * mm, "end": v(34.46, -30.6) * mm});
            skLineSegment(sketch, "E179.20.5", {"start": v(34.46, -30.6) * mm, "end": v(33.8, -30.43) * mm});
            skArc(sketch, "E179.20.6", {"start": v(33.8, -30.43) * mm, "mid": v(32.15, -30.42) * mm, "end": v(30.7, -31.23) * mm});
            skArc(sketch, "E179.21.0", {"start": v(40.54, -16.6) * mm, "mid": v(40.33, -17.34) * mm, "end": v(40.31, -18.11) * mm});
            skArc(sketch, "E179.21.1", {"start": v(40.31, -18.11) * mm, "mid": v(40.52, -18.98) * mm, "end": v(40.96, -19.76) * mm});
            skLineSegment(sketch, "E179.21.2", {"start": v(43.02, -22.43) * mm, "end": v(40.96, -19.76) * mm});
            skArc(sketch, "E179.21.3", {"start": v(42.58, -23.22) * mm, "mid": v(42.8, -22.82) * mm, "end": v(43.01, -22.41) * mm});
            skLineSegment(sketch, "E179.21.4", {"start": v(42.6, -23.22) * mm, "end": v(39.92, -23.05) * mm});
            skLineSegment(sketch, "E179.21.5", {"start": v(39.92, -23.05) * mm, "end": v(39.23, -23) * mm});
            skArc(sketch, "E179.21.6", {"start": v(39.23, -23) * mm, "mid": v(37.61, -23.32) * mm, "end": v(36.37, -24.41) * mm});
            skArc(sketch, "E179.22.0", {"start": v(43.05, -8.1) * mm, "mid": v(43, -8.86) * mm, "end": v(43.13, -9.63) * mm});
            skArc(sketch, "E179.22.1", {"start": v(43.13, -9.63) * mm, "mid": v(43.51, -10.43) * mm, "end": v(44.1, -11.1) * mm});
            skLineSegment(sketch, "E179.22.2", {"start": v(46.65, -13.3) * mm, "end": v(44.1, -11.1) * mm});
            skArc(sketch, "E179.22.3", {"start": v(46.38, -14.17) * mm, "mid": v(46.51, -13.73) * mm, "end": v(46.64, -13.3) * mm});
            skLineSegment(sketch, "E179.22.4", {"start": v(46.4, -14.17) * mm, "end": v(43.74, -14.54) * mm});
            skLineSegment(sketch, "E179.22.5", {"start": v(43.74, -14.54) * mm, "end": v(43.06, -14.63) * mm});
            skArc(sketch, "E179.22.6", {"start": v(43.06, -14.63) * mm, "mid": v(41.54, -15.27) * mm, "end": v(40.54, -16.6) * mm});
            skArc(sketch, "E179.23.0", {"start": v(43.8, 0.74) * mm, "mid": v(43.9, -0.03) * mm, "end": v(44.19, -0.75) * mm});
            skArc(sketch, "E179.23.1", {"start": v(44.19, -0.75) * mm, "mid": v(44.72, -1.46) * mm, "end": v(45.43, -2) * mm});
            skLineSegment(sketch, "E179.23.2", {"start": v(48.38, -3.64) * mm, "end": v(45.43, -2) * mm});
            skArc(sketch, "E179.23.3", {"start": v(48.29, -4.55) * mm, "mid": v(48.33, -4.1) * mm, "end": v(48.36, -3.64) * mm});
            skLineSegment(sketch, "E179.23.4", {"start": v(48.3, -4.54) * mm, "end": v(45.77, -5.44) * mm});
            skLineSegment(sketch, "E179.23.5", {"start": v(45.77, -5.44) * mm, "end": v(45.12, -5.67) * mm});
            skArc(sketch, "E179.23.6", {"start": v(45.12, -5.67) * mm, "mid": v(43.76, -6.6) * mm, "end": v(43.05, -8.1) * mm});
            skArc(sketch, "E179.24.0", {"start": v(42.75, 9.54) * mm, "mid": v(43, 8.81) * mm, "end": v(43.43, 8.16) * mm});
            skArc(sketch, "E179.24.1", {"start": v(43.43, 8.16) * mm, "mid": v(44.1, 7.57) * mm, "end": v(44.9, 7.19) * mm});
            skLineSegment(sketch, "E179.24.2", {"start": v(48.12, 6.17) * mm, "end": v(44.9, 7.19) * mm});
            skArc(sketch, "E179.24.3", {"start": v(48.21, 5.27) * mm, "mid": v(48.16, 5.72) * mm, "end": v(48.1, 6.17) * mm});
            skLineSegment(sketch, "E179.24.4", {"start": v(48.23, 5.28) * mm, "end": v(45.93, 3.89) * mm});
            skLineSegment(sketch, "E179.24.5", {"start": v(45.93, 3.89) * mm, "end": v(45.34, 3.53) * mm});
            skArc(sketch, "E179.24.6", {"start": v(45.34, 3.53) * mm, "mid": v(44.2, 2.34) * mm, "end": v(43.8, 0.74) * mm});
            skArc(sketch, "E179.25.0", {"start": v(39.95, 17.95) * mm, "mid": v(40.35, 17.29) * mm, "end": v(40.9, 16.74) * mm});
            skArc(sketch, "E179.25.1", {"start": v(40.9, 16.74) * mm, "mid": v(41.67, 16.3) * mm, "end": v(42.54, 16.08) * mm});
            skLineSegment(sketch, "E179.25.2", {"start": v(45.9, 15.73) * mm, "end": v(42.54, 16.08) * mm});
            skArc(sketch, "E179.25.3", {"start": v(46.17, 14.87) * mm, "mid": v(46.02, 15.3) * mm, "end": v(45.88, 15.73) * mm});
            skLineSegment(sketch, "E179.25.4", {"start": v(46.18, 14.88) * mm, "end": v(44.2, 13.05) * mm});
            skLineSegment(sketch, "E179.25.5", {"start": v(44.2, 13.05) * mm, "end": v(43.7, 12.59) * mm});
            skArc(sketch, "E179.25.6", {"start": v(43.7, 12.59) * mm, "mid": v(42.82, 11.2) * mm, "end": v(42.75, 9.54) * mm});
            skArc(sketch, "E179.26.0", {"start": v(35.52, 25.63) * mm, "mid": v(36.05, 25.06) * mm, "end": v(36.7, 24.63) * mm});
            skArc(sketch, "E179.26.1", {"start": v(36.7, 24.63) * mm, "mid": v(37.54, 24.35) * mm, "end": v(38.43, 24.31) * mm});
            skLineSegment(sketch, "E179.26.2", {"start": v(41.79, 24.65) * mm, "end": v(38.43, 24.31) * mm});
            skArc(sketch, "E179.26.3", {"start": v(42.23, 23.85) * mm, "mid": v(42, 24.25) * mm, "end": v(41.77, 24.65) * mm});
            skLineSegment(sketch, "E179.26.4", {"start": v(42.24, 23.87) * mm, "end": v(40.67, 21.68) * mm});
            skLineSegment(sketch, "E179.26.5", {"start": v(40.67, 21.68) * mm, "end": v(40.27, 21.13) * mm});
            skArc(sketch, "E179.26.6", {"start": v(40.27, 21.13) * mm, "mid": v(39.69, 19.58) * mm, "end": v(39.95, 17.95) * mm});
            skArc(sketch, "E179.27.0", {"start": v(29.64, 32.25) * mm, "mid": v(30.27, 31.8) * mm, "end": v(30.99, 31.51) * mm});
            skArc(sketch, "E179.27.1", {"start": v(30.99, 31.51) * mm, "mid": v(31.87, 31.4) * mm, "end": v(32.75, 31.55) * mm});
            skLineSegment(sketch, "E179.27.2", {"start": v(35.97, 32.55) * mm, "end": v(32.75, 31.55) * mm});
            skArc(sketch, "E179.27.3", {"start": v(36.56, 31.87) * mm, "mid": v(36.26, 32.2) * mm, "end": v(35.96, 32.55) * mm});
            skLineSegment(sketch, "E179.27.4", {"start": v(36.57, 31.88) * mm, "end": v(35.47, 29.43) * mm});
            skLineSegment(sketch, "E179.27.5", {"start": v(35.47, 29.43) * mm, "end": v(35.2, 28.8) * mm});
            skArc(sketch, "E179.27.6", {"start": v(35.2, 28.8) * mm, "mid": v(34.93, 27.17) * mm, "end": v(35.52, 25.63) * mm});
            skArc(sketch, "E179.28.0", {"start": v(22.54, 37.56) * mm, "mid": v(23.25, 37.24) * mm, "end": v(24, 37.1) * mm});
            skArc(sketch, "E179.28.1", {"start": v(24, 37.1) * mm, "mid": v(24.9, 37.18) * mm, "end": v(25.73, 37.5) * mm});
            skLineSegment(sketch, "E179.28.2", {"start": v(28.68, 39.13) * mm, "end": v(25.73, 37.5) * mm});
            skArc(sketch, "E179.28.3", {"start": v(29.4, 38.57) * mm, "mid": v(29.03, 38.85) * mm, "end": v(28.67, 39.12) * mm});
            skLineSegment(sketch, "E179.28.4", {"start": v(29.4, 38.59) * mm, "end": v(28.82, 35.97) * mm});
            skLineSegment(sketch, "E179.28.5", {"start": v(28.82, 35.97) * mm, "end": v(28.68, 35.3) * mm});
            skArc(sketch, "E179.28.6", {"start": v(28.68, 35.3) * mm, "mid": v(28.75, 33.65) * mm, "end": v(29.64, 32.25) * mm});
            skArc(sketch, "E179.29.0", {"start": v(14.52, 41.32) * mm, "mid": v(15.27, 41.16) * mm, "end": v(16.05, 41.18) * mm});
            skArc(sketch, "E179.29.1", {"start": v(16.05, 41.18) * mm, "mid": v(16.9, 41.43) * mm, "end": v(17.66, 41.91) * mm});
            skLineSegment(sketch, "E179.29.2", {"start": v(20.22, 44.1) * mm, "end": v(17.66, 41.91) * mm});
            skArc(sketch, "E179.29.3", {"start": v(21.03, 43.7) * mm, "mid": v(20.62, 43.9) * mm, "end": v(20.2, 44.1) * mm});
            skLineSegment(sketch, "E179.29.4", {"start": v(21.03, 43.72) * mm, "end": v(21, 41.03) * mm});
            skLineSegment(sketch, "E179.29.5", {"start": v(21, 41.03) * mm, "end": v(20.98, 40.35) * mm});
            skArc(sketch, "E179.29.6", {"start": v(20.98, 40.35) * mm, "mid": v(21.39, 38.74) * mm, "end": v(22.54, 37.56) * mm});
            skArc(sketch, "E179.30.0", {"start": v(5.9, 43.4) * mm, "mid": v(6.67, 43.4) * mm, "end": v(7.43, 43.57) * mm});
            skArc(sketch, "E179.30.1", {"start": v(7.43, 43.57) * mm, "mid": v(8.22, 43.99) * mm, "end": v(8.86, 44.6) * mm});
            skLineSegment(sketch, "E179.30.2", {"start": v(10.93, 47.27) * mm, "end": v(8.86, 44.6) * mm});
            skArc(sketch, "E179.30.3", {"start": v(11.8, 47.04) * mm, "mid": v(11.36, 47.15) * mm, "end": v(10.92, 47.26) * mm});
            skLineSegment(sketch, "E179.30.4", {"start": v(11.8, 47.06) * mm, "end": v(12.3, 44.42) * mm});
            skLineSegment(sketch, "E179.30.5", {"start": v(12.3, 44.42) * mm, "end": v(12.43, 43.74) * mm});
            skArc(sketch, "E179.30.6", {"start": v(12.43, 43.74) * mm, "mid": v(13.15, 42.26) * mm, "end": v(14.52, 41.32) * mm});
            skCircle(sketch, "E180", {"center": v(0, 0) * mm, "radius": 51.31 * mm});
            skSolve(sketch);
        }
        {
            var Q0;
            Q0 = qSketchRegion(id + "F8", true);
            extrude(context, id + "F9", {"entities" : qUnion([Q0]), "operationType" : NewBodyOperationType.REMOVE, "oppositeDirection" : true, "depth" : 6 * mm, "offsetDistance" : 25 * mm});
        }
        {
            var Q0;
            Q0=makeQuery(id+"F1.opRevolve","SWEPT_FACE",FACE,{"disambiguationData":[OSD([sQuery(id+"F0.wireOp",EDGE,"E13.MirrorCS")])]});
            var sketch = newSketch(context, id + "F10", { "sketchPlane" : qUnion([Q0])});
            skArc(sketch, "E181", {"start": v(-1.18, 48.49) * mm, "mid": v(-1.64, 48.47) * mm, "end": v(-2.1, 48.45) * mm});
            skArc(sketch, "E182", {"start": v(-5.9, 43.4) * mm, "mid": v(-4.38, 44.04) * mm, "end": v(-3.37, 45.35) * mm});
            skArc(sketch, "E183", {"start": v(0.3, 45.48) * mm, "mid": v(1.4, 44.23) * mm, "end": v(2.96, 43.7) * mm});
            skLineSegment(sketch, "E184", {"start": v(-2.09, 48.47) * mm, "end": v(-3.11, 45.99) * mm});
            skLineSegment(sketch, "E185", {"start": v(-3.11, 45.99) * mm, "end": v(-3.37, 45.35) * mm});
            skLineSegment(sketch, "E186", {"start": v(-1.19, 48.5) * mm, "end": v(0, 46.1) * mm});
            skLineSegment(sketch, "E187", {"start": v(0, 46.1) * mm, "end": v(0.3, 45.48) * mm});
            skArc(sketch, "E188.1.0", {"start": v(-14.52, 41.32) * mm, "mid": v(-13.15, 42.26) * mm, "end": v(-12.43, 43.75) * mm});
            skLineSegment(sketch, "E188.1.1", {"start": v(-12.3, 44.42) * mm, "end": v(-12.43, 43.75) * mm});
            skLineSegment(sketch, "E188.1.2", {"start": v(-11.8, 47.06) * mm, "end": v(-12.3, 44.42) * mm});
            skArc(sketch, "E188.1.3", {"start": v(-10.92, 47.26) * mm, "mid": v(-11.36, 47.15) * mm, "end": v(-11.8, 47.04) * mm});
            skLineSegment(sketch, "E188.1.4", {"start": v(-10.93, 47.27) * mm, "end": v(-9.28, 45.15) * mm});
            skLineSegment(sketch, "E188.1.5", {"start": v(-9.28, 45.15) * mm, "end": v(-8.86, 44.6) * mm});
            skArc(sketch, "E188.1.6", {"start": v(-8.86, 44.6) * mm, "mid": v(-7.54, 43.6) * mm, "end": v(-5.9, 43.4) * mm});
            skArc(sketch, "E188.2.0", {"start": v(-22.54, 37.56) * mm, "mid": v(-21.39, 38.74) * mm, "end": v(-20.98, 40.35) * mm});
            skLineSegment(sketch, "E188.2.1", {"start": v(-21, 41.03) * mm, "end": v(-20.98, 40.35) * mm});
            skLineSegment(sketch, "E188.2.2", {"start": v(-21.03, 43.72) * mm, "end": v(-21, 41.03) * mm});
            skArc(sketch, "E188.2.3", {"start": v(-20.2, 44.1) * mm, "mid": v(-20.62, 43.9) * mm, "end": v(-21.03, 43.7) * mm});
            skLineSegment(sketch, "E188.2.4", {"start": v(-20.22, 44.1) * mm, "end": v(-18.18, 42.36) * mm});
            skLineSegment(sketch, "E188.2.5", {"start": v(-18.18, 42.36) * mm, "end": v(-17.65, 41.91) * mm});
            skArc(sketch, "E188.2.6", {"start": v(-17.65, 41.91) * mm, "mid": v(-16.16, 41.2) * mm, "end": v(-14.52, 41.32) * mm});
            skArc(sketch, "E188.3.0", {"start": v(-29.64, 32.25) * mm, "mid": v(-28.75, 33.65) * mm, "end": v(-28.68, 35.3) * mm});
            skLineSegment(sketch, "E188.3.1", {"start": v(-28.82, 35.97) * mm, "end": v(-28.68, 35.3) * mm});
            skLineSegment(sketch, "E188.3.2", {"start": v(-29.4, 38.59) * mm, "end": v(-28.82, 35.97) * mm});
            skArc(sketch, "E188.3.3", {"start": v(-28.67, 39.12) * mm, "mid": v(-29.04, 38.85) * mm, "end": v(-29.4, 38.57) * mm});
            skLineSegment(sketch, "E188.3.4", {"start": v(-28.68, 39.13) * mm, "end": v(-26.33, 37.83) * mm});
            skLineSegment(sketch, "E188.3.5", {"start": v(-26.33, 37.83) * mm, "end": v(-25.73, 37.5) * mm});
            skArc(sketch, "E188.3.6", {"start": v(-25.73, 37.5) * mm, "mid": v(-24.13, 37.1) * mm, "end": v(-22.54, 37.56) * mm});
            skArc(sketch, "E188.4.0", {"start": v(-35.52, 25.63) * mm, "mid": v(-34.93, 27.17) * mm, "end": v(-35.2, 28.8) * mm});
            skLineSegment(sketch, "E188.4.1", {"start": v(-35.47, 29.43) * mm, "end": v(-35.2, 28.8) * mm});
            skLineSegment(sketch, "E188.4.2", {"start": v(-36.57, 31.88) * mm, "end": v(-35.47, 29.43) * mm});
            skArc(sketch, "E188.4.3", {"start": v(-35.96, 32.55) * mm, "mid": v(-36.26, 32.2) * mm, "end": v(-36.56, 31.87) * mm});
            skLineSegment(sketch, "E188.4.4", {"start": v(-35.97, 32.55) * mm, "end": v(-33.4, 31.76) * mm});
            skLineSegment(sketch, "E188.4.5", {"start": v(-33.4, 31.76) * mm, "end": v(-32.75, 31.55) * mm});
            skArc(sketch, "E188.4.6", {"start": v(-32.75, 31.55) * mm, "mid": v(-31.1, 31.49) * mm, "end": v(-29.64, 32.25) * mm});
            skArc(sketch, "E188.5.0", {"start": v(-39.95, 17.95) * mm, "mid": v(-39.69, 19.58) * mm, "end": v(-40.27, 21.13) * mm});
            skLineSegment(sketch, "E188.5.1", {"start": v(-40.67, 21.68) * mm, "end": v(-40.27, 21.13) * mm});
            skLineSegment(sketch, "E188.5.2", {"start": v(-42.24, 23.87) * mm, "end": v(-40.67, 21.68) * mm});
            skArc(sketch, "E188.5.3", {"start": v(-41.77, 24.64) * mm, "mid": v(-42, 24.25) * mm, "end": v(-42.23, 23.85) * mm});
            skLineSegment(sketch, "E188.5.4", {"start": v(-41.79, 24.65) * mm, "end": v(-39.12, 24.38) * mm});
            skLineSegment(sketch, "E188.5.5", {"start": v(-39.12, 24.38) * mm, "end": v(-38.43, 24.31) * mm});
            skArc(sketch, "E188.5.6", {"start": v(-38.43, 24.31) * mm, "mid": v(-36.8, 24.58) * mm, "end": v(-35.52, 25.63) * mm});
            skArc(sketch, "E188.6.0", {"start": v(-42.75, 9.54) * mm, "mid": v(-42.82, 11.2) * mm, "end": v(-43.7, 12.59) * mm});
            skLineSegment(sketch, "E188.6.1", {"start": v(-44.2, 13.05) * mm, "end": v(-43.7, 12.59) * mm});
            skLineSegment(sketch, "E188.6.2", {"start": v(-46.18, 14.87) * mm, "end": v(-44.2, 13.05) * mm});
            skArc(sketch, "E188.6.3", {"start": v(-45.88, 15.73) * mm, "mid": v(-46.02, 15.3) * mm, "end": v(-46.17, 14.86) * mm});
            skLineSegment(sketch, "E188.6.4", {"start": v(-45.9, 15.73) * mm, "end": v(-43.22, 16) * mm});
            skLineSegment(sketch, "E188.6.5", {"start": v(-43.22, 16) * mm, "end": v(-42.54, 16.08) * mm});
            skArc(sketch, "E188.6.6", {"start": v(-42.54, 16.08) * mm, "mid": v(-41, 16.67) * mm, "end": v(-39.95, 17.95) * mm});
            skArc(sketch, "E188.7.0", {"start": v(-43.8, 0.74) * mm, "mid": v(-44.2, 2.34) * mm, "end": v(-45.34, 3.53) * mm});
            skLineSegment(sketch, "E188.7.1", {"start": v(-45.93, 3.89) * mm, "end": v(-45.34, 3.53) * mm});
            skLineSegment(sketch, "E188.7.2", {"start": v(-48.23, 5.27) * mm, "end": v(-45.93, 3.89) * mm});
            skArc(sketch, "E188.7.3", {"start": v(-48.1, 6.17) * mm, "mid": v(-48.16, 5.72) * mm, "end": v(-48.21, 5.27) * mm});
            skLineSegment(sketch, "E188.7.4", {"start": v(-48.12, 6.17) * mm, "end": v(-45.56, 6.98) * mm});
            skLineSegment(sketch, "E188.7.5", {"start": v(-45.56, 6.98) * mm, "end": v(-44.9, 7.19) * mm});
            skArc(sketch, "E188.7.6", {"start": v(-44.9, 7.19) * mm, "mid": v(-43.51, 8.08) * mm, "end": v(-42.75, 9.54) * mm});
            skArc(sketch, "E188.8.0", {"start": v(-43.05, -8.1) * mm, "mid": v(-43.76, -6.6) * mm, "end": v(-45.12, -5.67) * mm});
            skLineSegment(sketch, "E188.8.1", {"start": v(-45.77, -5.44) * mm, "end": v(-45.12, -5.67) * mm});
            skLineSegment(sketch, "E188.8.2", {"start": v(-48.3, -4.54) * mm, "end": v(-45.77, -5.44) * mm});
            skArc(sketch, "E188.8.3", {"start": v(-48.36, -3.64) * mm, "mid": v(-48.33, -4.1) * mm, "end": v(-48.29, -4.55) * mm});
            skLineSegment(sketch, "E188.8.4", {"start": v(-48.38, -3.64) * mm, "end": v(-46.03, -2.33) * mm});
            skLineSegment(sketch, "E188.8.5", {"start": v(-46.03, -2.33) * mm, "end": v(-45.43, -2) * mm});
            skArc(sketch, "E188.8.6", {"start": v(-45.43, -2) * mm, "mid": v(-44.25, -0.85) * mm, "end": v(-43.8, 0.74) * mm});
            skArc(sketch, "E188.9.0", {"start": v(-40.54, -16.6) * mm, "mid": v(-41.54, -15.27) * mm, "end": v(-43.06, -14.63) * mm});
            skLineSegment(sketch, "E188.9.1", {"start": v(-43.74, -14.54) * mm, "end": v(-43.06, -14.63) * mm});
            skLineSegment(sketch, "E188.9.2", {"start": v(-46.4, -14.17) * mm, "end": v(-43.74, -14.54) * mm});
            skArc(sketch, "E188.9.3", {"start": v(-46.64, -13.3) * mm, "mid": v(-46.51, -13.74) * mm, "end": v(-46.38, -14.17) * mm});
            skLineSegment(sketch, "E188.9.4", {"start": v(-46.65, -13.3) * mm, "end": v(-44.62, -11.55) * mm});
            skLineSegment(sketch, "E188.9.5", {"start": v(-44.62, -11.55) * mm, "end": v(-44.1, -11.1) * mm});
            skArc(sketch, "E188.9.6", {"start": v(-44.1, -11.1) * mm, "mid": v(-43.17, -9.74) * mm, "end": v(-43.05, -8.1) * mm});
            skArc(sketch, "E188.10.0", {"start": v(-36.37, -24.41) * mm, "mid": v(-37.61, -23.32) * mm, "end": v(-39.23, -23) * mm});
            skLineSegment(sketch, "E188.10.1", {"start": v(-39.92, -23.05) * mm, "end": v(-39.23, -23) * mm});
            skLineSegment(sketch, "E188.10.2", {"start": v(-42.6, -23.22) * mm, "end": v(-39.92, -23.05) * mm});
            skArc(sketch, "E188.10.3", {"start": v(-43, -22.41) * mm, "mid": v(-42.8, -22.82) * mm, "end": v(-42.58, -23.22) * mm});
            skLineSegment(sketch, "E188.10.4", {"start": v(-43.02, -22.43) * mm, "end": v(-41.38, -20.3) * mm});
            skLineSegment(sketch, "E188.10.5", {"start": v(-41.38, -20.3) * mm, "end": v(-40.96, -19.75) * mm});
            skArc(sketch, "E188.10.6", {"start": v(-40.96, -19.75) * mm, "mid": v(-40.33, -18.23) * mm, "end": v(-40.54, -16.6) * mm});
            skArc(sketch, "E188.11.0", {"start": v(-30.7, -31.23) * mm, "mid": v(-32.15, -30.42) * mm, "end": v(-33.8, -30.43) * mm});
            skLineSegment(sketch, "E188.11.1", {"start": v(-34.46, -30.6) * mm, "end": v(-33.8, -30.43) * mm});
            skLineSegment(sketch, "E188.11.2", {"start": v(-37.05, -31.32) * mm, "end": v(-34.46, -30.6) * mm});
            skArc(sketch, "E188.11.3", {"start": v(-37.62, -30.61) * mm, "mid": v(-37.33, -30.97) * mm, "end": v(-37.03, -31.32) * mm});
            skLineSegment(sketch, "E188.11.4", {"start": v(-37.62, -30.63) * mm, "end": v(-36.45, -28.21) * mm});
            skLineSegment(sketch, "E188.11.5", {"start": v(-36.45, -28.21) * mm, "end": v(-36.15, -27.6) * mm});
            skArc(sketch, "E188.11.6", {"start": v(-36.15, -27.6) * mm, "mid": v(-35.83, -25.97) * mm, "end": v(-36.37, -24.41) * mm});
            skArc(sketch, "E188.12.0", {"start": v(-23.8, -36.77) * mm, "mid": v(-25.37, -36.26) * mm, "end": v(-26.98, -36.6) * mm});
            skLineSegment(sketch, "E188.12.1", {"start": v(-27.6, -36.92) * mm, "end": v(-26.98, -36.6) * mm});
            skLineSegment(sketch, "E188.12.2", {"start": v(-29.99, -38.14) * mm, "end": v(-27.6, -36.92) * mm});
            skArc(sketch, "E188.12.3", {"start": v(-30.69, -37.56) * mm, "mid": v(-30.33, -37.85) * mm, "end": v(-29.97, -38.13) * mm});
            skLineSegment(sketch, "E188.12.4", {"start": v(-30.69, -37.57) * mm, "end": v(-30.02, -34.97) * mm});
            skLineSegment(sketch, "E188.12.5", {"start": v(-30.02, -34.97) * mm, "end": v(-29.85, -34.3) * mm});
            skArc(sketch, "E188.12.6", {"start": v(-29.85, -34.3) * mm, "mid": v(-29.87, -32.66) * mm, "end": v(-30.7, -31.23) * mm});
            skArc(sketch, "E188.13.0", {"start": v(-15.9, -40.81) * mm, "mid": v(-17.55, -40.63) * mm, "end": v(-19.06, -41.3) * mm});
            skLineSegment(sketch, "E188.13.1", {"start": v(-19.6, -41.72) * mm, "end": v(-19.06, -41.3) * mm});
            skLineSegment(sketch, "E188.13.2", {"start": v(-21.7, -43.4) * mm, "end": v(-19.6, -41.72) * mm});
            skArc(sketch, "E188.13.3", {"start": v(-22.5, -42.97) * mm, "mid": v(-22.1, -43.18) * mm, "end": v(-21.68, -43.38) * mm});
            skLineSegment(sketch, "E188.13.4", {"start": v(-22.5, -42.98) * mm, "end": v(-22.37, -40.3) * mm});
            skLineSegment(sketch, "E188.13.5", {"start": v(-22.37, -40.3) * mm, "end": v(-22.34, -39.61) * mm});
            skArc(sketch, "E188.13.6", {"start": v(-22.34, -39.61) * mm, "mid": v(-22.68, -38) * mm, "end": v(-23.8, -36.77) * mm});
            skArc(sketch, "E188.14.0", {"start": v(-7.36, -43.18) * mm, "mid": v(-9, -43.33) * mm, "end": v(-10.36, -44.28) * mm});
            skLineSegment(sketch, "E188.14.1", {"start": v(-10.8, -44.8) * mm, "end": v(-10.36, -44.28) * mm});
            skLineSegment(sketch, "E188.14.2", {"start": v(-12.52, -46.87) * mm, "end": v(-10.8, -44.8) * mm});
            skArc(sketch, "E188.14.3", {"start": v(-13.39, -46.62) * mm, "mid": v(-12.95, -46.74) * mm, "end": v(-12.5, -46.86) * mm});
            skLineSegment(sketch, "E188.14.4", {"start": v(-13.38, -46.63) * mm, "end": v(-13.8, -43.98) * mm});
            skLineSegment(sketch, "E188.14.5", {"start": v(-13.8, -43.98) * mm, "end": v(-13.9, -43.3) * mm});
            skArc(sketch, "E188.14.6", {"start": v(-13.9, -43.3) * mm, "mid": v(-14.57, -41.79) * mm, "end": v(-15.9, -40.81) * mm});
            skArc(sketch, "E188.15.0", {"start": v(1.48, -43.78) * mm, "mid": v(-0.1, -44.26) * mm, "end": v(-1.23, -45.46) * mm});
            skLineSegment(sketch, "E188.15.1", {"start": v(-1.56, -46.07) * mm, "end": v(-1.23, -45.46) * mm});
            skLineSegment(sketch, "E188.15.2", {"start": v(-2.83, -48.43) * mm, "end": v(-1.56, -46.07) * mm});
            skArc(sketch, "E188.15.3", {"start": v(-3.73, -48.36) * mm, "mid": v(-3.27, -48.39) * mm, "end": v(-2.82, -48.42) * mm});
            skLineSegment(sketch, "E188.15.4", {"start": v(-3.72, -48.37) * mm, "end": v(-4.66, -45.85) * mm});
            skLineSegment(sketch, "E188.15.5", {"start": v(-4.66, -45.85) * mm, "end": v(-4.9, -45.21) * mm});
            skArc(sketch, "E188.15.6", {"start": v(-4.9, -45.21) * mm, "mid": v(-5.86, -43.87) * mm, "end": v(-7.36, -43.18) * mm});
            skArc(sketch, "E188.16.0", {"start": v(10.26, -42.58) * mm, "mid": v(8.8, -43.37) * mm, "end": v(7.94, -44.78) * mm});
            skLineSegment(sketch, "E188.16.1", {"start": v(7.75, -45.44) * mm, "end": v(7.94, -44.78) * mm});
            skLineSegment(sketch, "E188.16.2", {"start": v(6.98, -48) * mm, "end": v(7.75, -45.44) * mm});
            skArc(sketch, "E188.16.3", {"start": v(6.08, -48.12) * mm, "mid": v(6.53, -48.06) * mm, "end": v(6.99, -48) * mm});
            skLineSegment(sketch, "E188.16.4", {"start": v(6.09, -48.13) * mm, "end": v(4.66, -45.85) * mm});
            skLineSegment(sketch, "E188.16.5", {"start": v(4.66, -45.85) * mm, "end": v(4.3, -45.27) * mm});
            skArc(sketch, "E188.16.6", {"start": v(4.3, -45.27) * mm, "mid": v(3.09, -44.15) * mm, "end": v(1.48, -43.78) * mm});
            skArc(sketch, "E188.17.0", {"start": v(18.62, -39.64) * mm, "mid": v(17.36, -40.7) * mm, "end": v(16.8, -42.26) * mm});
            skLineSegment(sketch, "E188.17.1", {"start": v(16.74, -42.95) * mm, "end": v(16.8, -42.26) * mm});
            skLineSegment(sketch, "E188.17.2", {"start": v(16.5, -45.62) * mm, "end": v(16.74, -42.95) * mm});
            skArc(sketch, "E188.17.3", {"start": v(15.64, -45.9) * mm, "mid": v(16.07, -45.76) * mm, "end": v(16.5, -45.6) * mm});
            skLineSegment(sketch, "E188.17.4", {"start": v(15.65, -45.92) * mm, "end": v(13.8, -43.98) * mm});
            skLineSegment(sketch, "E188.17.5", {"start": v(13.8, -43.98) * mm, "end": v(13.32, -43.48) * mm});
            skArc(sketch, "E188.17.6", {"start": v(13.32, -43.48) * mm, "mid": v(11.91, -42.62) * mm, "end": v(10.26, -42.58) * mm});
            skArc(sketch, "E188.18.0", {"start": v(26.22, -35.08) * mm, "mid": v(25.2, -36.38) * mm, "end": v(24.96, -38.02) * mm});
            skLineSegment(sketch, "E188.18.1", {"start": v(25.04, -38.7) * mm, "end": v(24.96, -38.02) * mm});
            skLineSegment(sketch, "E188.18.2", {"start": v(25.35, -41.37) * mm, "end": v(25.04, -38.7) * mm});
            skArc(sketch, "E188.18.3", {"start": v(24.56, -41.82) * mm, "mid": v(24.96, -41.59) * mm, "end": v(25.35, -41.35) * mm});
            skLineSegment(sketch, "E188.18.4", {"start": v(24.58, -41.83) * mm, "end": v(22.37, -40.3) * mm});
            skLineSegment(sketch, "E188.18.5", {"start": v(22.37, -40.3) * mm, "end": v(21.8, -39.9) * mm});
            skArc(sketch, "E188.18.6", {"start": v(21.8, -39.9) * mm, "mid": v(20.25, -39.35) * mm, "end": v(18.62, -39.64) * mm});
            skArc(sketch, "E188.19.0", {"start": v(32.75, -29.09) * mm, "mid": v(32, -30.56) * mm, "end": v(32.1, -32.22) * mm});
            skLineSegment(sketch, "E188.19.1", {"start": v(32.32, -32.87) * mm, "end": v(32.1, -32.22) * mm});
            skLineSegment(sketch, "E188.19.2", {"start": v(33.16, -35.42) * mm, "end": v(32.32, -32.87) * mm});
            skArc(sketch, "E188.19.3", {"start": v(32.48, -36.02) * mm, "mid": v(32.82, -35.71) * mm, "end": v(33.15, -35.4) * mm});
            skLineSegment(sketch, "E188.19.4", {"start": v(32.5, -36.03) * mm, "end": v(30.02, -34.97) * mm});
            skLineSegment(sketch, "E188.19.5", {"start": v(30.02, -34.97) * mm, "end": v(29.4, -34.7) * mm});
            skArc(sketch, "E188.19.6", {"start": v(29.4, -34.7) * mm, "mid": v(27.76, -34.47) * mm, "end": v(26.22, -35.08) * mm});
            skArc(sketch, "E188.20.0", {"start": v(37.93, -21.9) * mm, "mid": v(37.5, -23.5) * mm, "end": v(37.93, -25.1) * mm});
            skLineSegment(sketch, "E188.20.1", {"start": v(38.27, -25.69) * mm, "end": v(37.93, -25.1) * mm});
            skLineSegment(sketch, "E188.20.2", {"start": v(39.6, -28.02) * mm, "end": v(38.27, -25.69) * mm});
            skArc(sketch, "E188.20.3", {"start": v(39.06, -28.74) * mm, "mid": v(39.33, -28.37) * mm, "end": v(39.6, -28) * mm});
            skLineSegment(sketch, "E188.20.4", {"start": v(39.08, -28.75) * mm, "end": v(36.45, -28.21) * mm});
            skLineSegment(sketch, "E188.20.5", {"start": v(36.45, -28.21) * mm, "end": v(35.78, -28.08) * mm});
            skArc(sketch, "E188.20.6", {"start": v(35.78, -28.08) * mm, "mid": v(34.13, -28.18) * mm, "end": v(32.75, -29.09) * mm});
            skArc(sketch, "E188.21.0", {"start": v(41.56, -13.82) * mm, "mid": v(41.47, -15.47) * mm, "end": v(42.2, -16.95) * mm});
            skLineSegment(sketch, "E188.21.1", {"start": v(42.66, -17.46) * mm, "end": v(42.2, -16.95) * mm});
            skLineSegment(sketch, "E188.21.2", {"start": v(44.44, -19.47) * mm, "end": v(42.66, -17.46) * mm});
            skArc(sketch, "E188.21.3", {"start": v(44.05, -20.3) * mm, "mid": v(44.24, -19.88) * mm, "end": v(44.43, -19.46) * mm});
            skLineSegment(sketch, "E188.21.4", {"start": v(44.07, -20.3) * mm, "end": v(41.38, -20.3) * mm});
            skLineSegment(sketch, "E188.21.5", {"start": v(41.38, -20.3) * mm, "end": v(40.7, -20.3) * mm});
            skArc(sketch, "E188.21.6", {"start": v(40.7, -20.3) * mm, "mid": v(39.1, -20.73) * mm, "end": v(37.93, -21.9) * mm});
            skArc(sketch, "E188.22.0", {"start": v(43.5, -5.17) * mm, "mid": v(43.73, -6.8) * mm, "end": v(44.75, -8.1) * mm});
            skLineSegment(sketch, "E188.22.1", {"start": v(45.3, -8.51) * mm, "end": v(44.75, -8.1) * mm});
            skLineSegment(sketch, "E188.22.2", {"start": v(47.45, -10.13) * mm, "end": v(45.3, -8.51) * mm});
            skArc(sketch, "E188.22.3", {"start": v(47.23, -11) * mm, "mid": v(47.34, -10.56) * mm, "end": v(47.43, -10.12) * mm});
            skLineSegment(sketch, "E188.22.4", {"start": v(47.25, -11) * mm, "end": v(44.62, -11.55) * mm});
            skLineSegment(sketch, "E188.22.5", {"start": v(44.62, -11.55) * mm, "end": v(43.95, -11.7) * mm});
            skArc(sketch, "E188.22.6", {"start": v(43.95, -11.7) * mm, "mid": v(42.47, -12.44) * mm, "end": v(41.56, -13.82) * mm});
            skArc(sketch, "E188.23.0", {"start": v(43.64, 3.7) * mm, "mid": v(44.2, 2.14) * mm, "end": v(45.47, 1.07) * mm});
            skLineSegment(sketch, "E188.23.1", {"start": v(46.08, 0.78) * mm, "end": v(45.47, 1.07) * mm});
            skLineSegment(sketch, "E188.23.2", {"start": v(48.51, -0.37) * mm, "end": v(46.08, 0.78) * mm});
            skArc(sketch, "E188.23.3", {"start": v(48.48, -1.28) * mm, "mid": v(48.5, -0.82) * mm, "end": v(48.5, -0.36) * mm});
            skLineSegment(sketch, "E188.23.4", {"start": v(48.5, -1.27) * mm, "end": v(46.03, -2.33) * mm});
            skLineSegment(sketch, "E188.23.5", {"start": v(46.03, -2.33) * mm, "end": v(45.4, -2.6) * mm});
            skArc(sketch, "E188.23.6", {"start": v(45.4, -2.6) * mm, "mid": v(44.1, -3.63) * mm, "end": v(43.5, -5.17) * mm});
            skArc(sketch, "E188.24.0", {"start": v(42, 12.4) * mm, "mid": v(42.87, 11) * mm, "end": v(44.32, 10.2) * mm});
            skLineSegment(sketch, "E188.24.1", {"start": v(44.98, 10.04) * mm, "end": v(44.32, 10.2) * mm});
            skLineSegment(sketch, "E188.24.2", {"start": v(47.6, 9.4) * mm, "end": v(44.98, 10.04) * mm});
            skArc(sketch, "E188.24.3", {"start": v(47.75, 8.51) * mm, "mid": v(47.67, 8.96) * mm, "end": v(47.58, 9.4) * mm});
            skLineSegment(sketch, "E188.24.4", {"start": v(47.76, 8.52) * mm, "end": v(45.56, 6.98) * mm});
            skLineSegment(sketch, "E188.24.5", {"start": v(45.56, 6.98) * mm, "end": v(45, 6.59) * mm});
            skArc(sketch, "E188.24.6", {"start": v(45, 6.59) * mm, "mid": v(43.93, 5.32) * mm, "end": v(43.64, 3.7) * mm});
            skArc(sketch, "E188.25.0", {"start": v(38.65, 20.6) * mm, "mid": v(39.78, 19.4) * mm, "end": v(41.36, 18.91) * mm});
            skLineSegment(sketch, "E188.25.1", {"start": v(42.04, 18.89) * mm, "end": v(41.36, 18.91) * mm});
            skLineSegment(sketch, "E188.25.2", {"start": v(44.73, 18.8) * mm, "end": v(42.04, 18.89) * mm});
            skArc(sketch, "E188.25.3", {"start": v(45.06, 17.95) * mm, "mid": v(44.89, 18.37) * mm, "end": v(44.71, 18.8) * mm});
            skLineSegment(sketch, "E188.25.4", {"start": v(45.07, 17.96) * mm, "end": v(43.22, 16) * mm});
            skLineSegment(sketch, "E188.25.5", {"start": v(43.22, 16) * mm, "end": v(42.75, 15.5) * mm});
            skArc(sketch, "E188.25.6", {"start": v(42.75, 15.5) * mm, "mid": v(41.96, 14.06) * mm, "end": v(42, 12.4) * mm});
            skArc(sketch, "E188.26.0", {"start": v(33.71, 27.96) * mm, "mid": v(35.06, 27) * mm, "end": v(36.7, 26.85) * mm});
            skLineSegment(sketch, "E188.26.1", {"start": v(37.38, 26.97) * mm, "end": v(36.7, 26.85) * mm});
            skLineSegment(sketch, "E188.26.2", {"start": v(40.03, 27.41) * mm, "end": v(37.38, 26.97) * mm});
            skArc(sketch, "E188.26.3", {"start": v(40.52, 26.65) * mm, "mid": v(40.27, 27.03) * mm, "end": v(40.01, 27.4) * mm});
            skLineSegment(sketch, "E188.26.4", {"start": v(40.53, 26.66) * mm, "end": v(39.12, 24.38) * mm});
            skLineSegment(sketch, "E188.26.5", {"start": v(39.12, 24.38) * mm, "end": v(38.75, 23.8) * mm});
            skArc(sketch, "E188.26.6", {"start": v(38.75, 23.8) * mm, "mid": v(38.28, 22.22) * mm, "end": v(38.65, 20.6) * mm});
            skArc(sketch, "E188.27.0", {"start": v(27.4, 34.18) * mm, "mid": v(28.9, 33.51) * mm, "end": v(30.55, 33.7) * mm});
            skLineSegment(sketch, "E188.27.1", {"start": v(31.19, 33.94) * mm, "end": v(30.55, 33.7) * mm});
            skLineSegment(sketch, "E188.27.2", {"start": v(33.7, 34.9) * mm, "end": v(31.19, 33.94) * mm});
            skArc(sketch, "E188.27.3", {"start": v(34.33, 34.26) * mm, "mid": v(34, 34.58) * mm, "end": v(33.68, 34.9) * mm});
            skLineSegment(sketch, "E188.27.4", {"start": v(34.33, 34.28) * mm, "end": v(33.4, 31.76) * mm});
            skLineSegment(sketch, "E188.27.5", {"start": v(33.4, 31.76) * mm, "end": v(33.17, 31.11) * mm});
            skArc(sketch, "E188.27.6", {"start": v(33.17, 31.11) * mm, "mid": v(33.02, 29.47) * mm, "end": v(33.71, 27.96) * mm});
            skArc(sketch, "E188.28.0", {"start": v(19.95, 39) * mm, "mid": v(21.57, 38.65) * mm, "end": v(23.14, 39.15) * mm});
            skLineSegment(sketch, "E188.28.1", {"start": v(23.72, 39.52) * mm, "end": v(23.14, 39.15) * mm});
            skLineSegment(sketch, "E188.28.2", {"start": v(25.97, 40.98) * mm, "end": v(23.72, 39.52) * mm});
            skArc(sketch, "E188.28.3", {"start": v(26.73, 40.47) * mm, "mid": v(26.35, 40.72) * mm, "end": v(25.96, 40.97) * mm});
            skLineSegment(sketch, "E188.28.4", {"start": v(26.73, 40.49) * mm, "end": v(26.33, 37.83) * mm});
            skLineSegment(sketch, "E188.28.5", {"start": v(26.33, 37.83) * mm, "end": v(26.23, 37.15) * mm});
            skArc(sketch, "E188.28.6", {"start": v(26.23, 37.15) * mm, "mid": v(26.41, 35.5) * mm, "end": v(27.4, 34.18) * mm});
            skArc(sketch, "E188.29.0", {"start": v(11.7, 42.21) * mm, "mid": v(13.35, 42.2) * mm, "end": v(14.79, 43) * mm});
            skLineSegment(sketch, "E188.29.1", {"start": v(15.28, 43.49) * mm, "end": v(14.79, 43) * mm});
            skLineSegment(sketch, "E188.29.2", {"start": v(17.2, 45.37) * mm, "end": v(15.28, 43.49) * mm});
            skArc(sketch, "E188.29.3", {"start": v(18.03, 45.02) * mm, "mid": v(17.6, 45.2) * mm, "end": v(17.18, 45.35) * mm});
            skLineSegment(sketch, "E188.29.4", {"start": v(18.03, 45.04) * mm, "end": v(18.18, 42.36) * mm});
            skLineSegment(sketch, "E188.29.5", {"start": v(18.18, 42.36) * mm, "end": v(18.21, 41.67) * mm});
            skArc(sketch, "E188.29.6", {"start": v(18.21, 41.67) * mm, "mid": v(18.72, 40.1) * mm, "end": v(19.95, 39) * mm});
            skArc(sketch, "E188.30.0", {"start": v(2.96, 43.7) * mm, "mid": v(4.58, 44.02) * mm, "end": v(5.83, 45.1) * mm});
            skLineSegment(sketch, "E188.30.1", {"start": v(6.2, 45.67) * mm, "end": v(5.83, 45.1) * mm});
            skLineSegment(sketch, "E188.30.2", {"start": v(7.71, 47.9) * mm, "end": v(6.2, 45.67) * mm});
            skArc(sketch, "E188.30.3", {"start": v(8.6, 47.73) * mm, "mid": v(8.15, 47.8) * mm, "end": v(7.7, 47.88) * mm});
            skLineSegment(sketch, "E188.30.4", {"start": v(8.6, 47.75) * mm, "end": v(9.28, 45.15) * mm});
            skLineSegment(sketch, "E188.30.5", {"start": v(9.28, 45.15) * mm, "end": v(9.45, 44.48) * mm});
            skArc(sketch, "E188.30.6", {"start": v(9.45, 44.48) * mm, "mid": v(10.27, 43.05) * mm, "end": v(11.7, 42.21) * mm});
            skCircle(sketch, "E189", {"center": v(0, 0) * mm, "radius": 51.88 * mm});
            skSolve(sketch);
        }
        {
            var Q0;
            Q0 = qSketchRegion(id + "F10", true);
            extrude(context, id + "F11", {"entities" : qUnion([Q0]), "operationType" : NewBodyOperationType.REMOVE, "oppositeDirection" : true, "depth" : 6 * mm, "offsetDistance" : 25 * mm});
        }
    });
